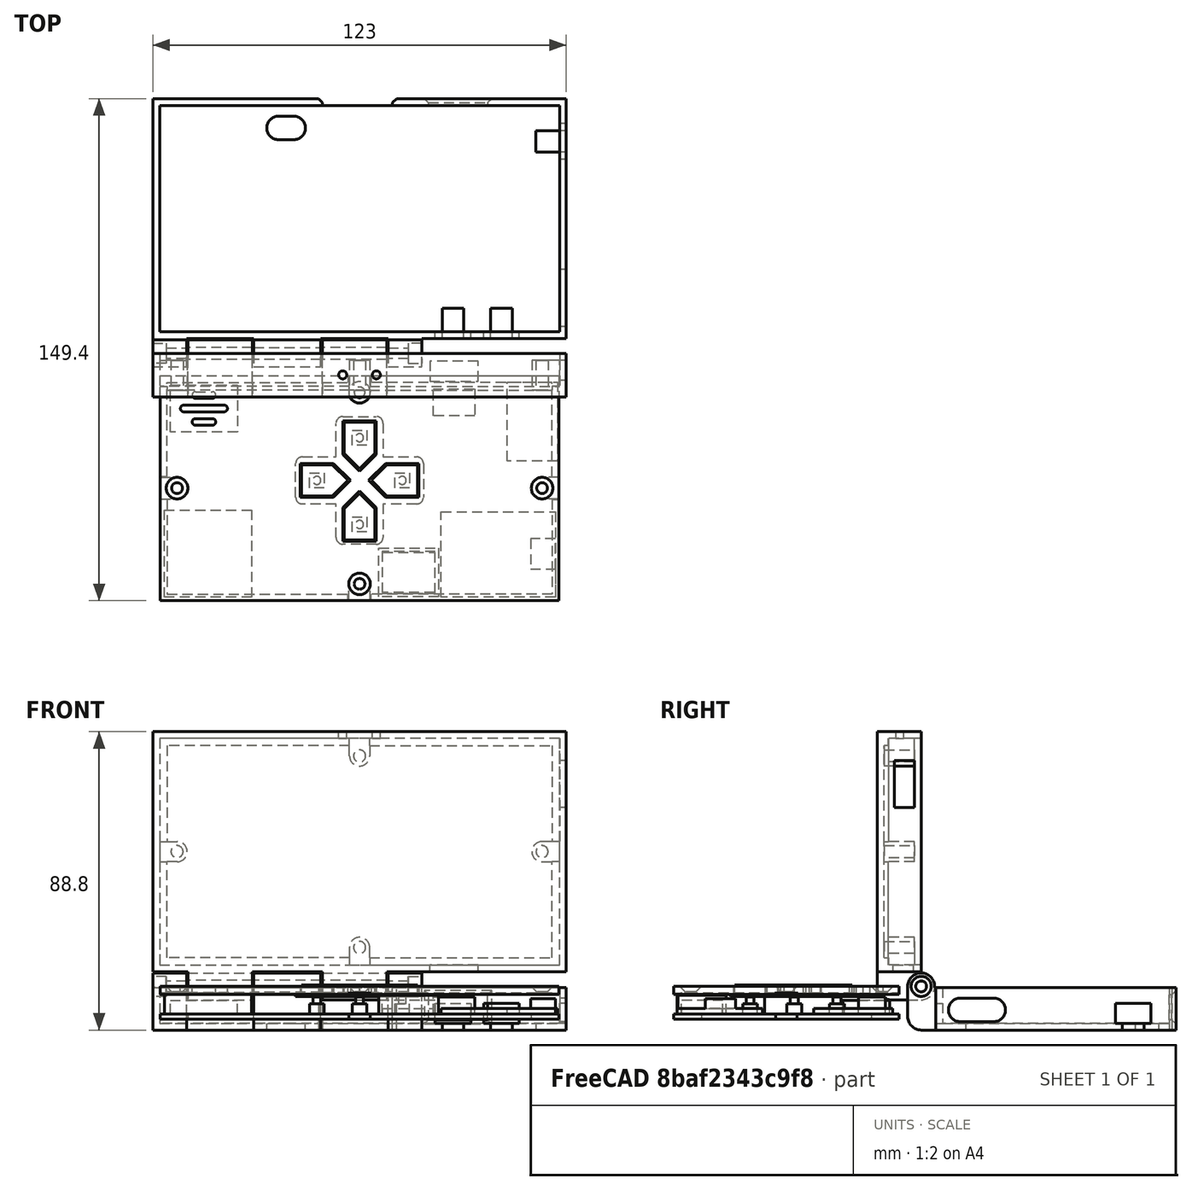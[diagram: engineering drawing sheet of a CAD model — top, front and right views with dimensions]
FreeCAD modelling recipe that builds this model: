
FCSTD DOCUMENT  (FreeCAD 0.19R24276 (Git))
Label: M3
License: All rights reserved
LicenseURL: http://en.wikipedia.org/wiki/All_rights_reserved
objects: Sketcher::SketchObject×45, PartDesign::Pocket×20, PartDesign::ShapeBinder×18, PartDesign::Pad×16, PartDesign::Body×7, TechDraw::DrawViewDimension×6, TechDraw::DrawViewPart×5, Mesh::Feature×5, TechDraw::DrawSVGTemplate×2, PartDesign::Chamfer×2, TechDraw::DrawPage×2
note: 146 computed .brp shape members not serialized (recipe doc carries the construction recipe); baked Part::Feature solids carry a one-line shape summary decoded from their .brp

FEATURE [TechDraw::DrawSVGTemplate] Template
  EditableTexts = Designed_by_Name=Designed by Name; Drawing_number=Drawing number; FC-Date=Date; FC-SC=Scale; FC-SH=Sheet; FC-Title=Title; Subtitle=Subtitle; Weight=Weight
  Height = 210
  Orientation = 1
  Width = 297
FEATURE [Sketcher::SketchObject] Sketch  label="Workspace"
  FullyConstrained = true
  MapMode = 5
  Support = -> [XY_Plane]
  sketch-geometry (8):
    g0: LineSegment StartX=-59.3 StartY=-6.6 StartZ=0 EndX=59.3 EndY=-6.6 EndZ=0
    g1: LineSegment StartX=59.3 StartY=-6.6 StartZ=0 EndX=59.3 EndY=-73.6 EndZ=0
    g2: LineSegment StartX=59.3 StartY=-73.6 StartZ=0 EndX=-59.3 EndY=-73.6 EndZ=0
    g3: LineSegment StartX=-59.3 StartY=-73.6 StartZ=0 EndX=-59.3 EndY=-6.6 EndZ=0
    g4: LineSegment StartX=-59.3 StartY=73.6 StartZ=0 EndX=59.3 EndY=73.6 EndZ=0
    g5: LineSegment StartX=59.3 StartY=73.6 StartZ=0 EndX=59.3 EndY=6.6 EndZ=0
    g6: LineSegment StartX=59.3 StartY=6.6 StartZ=0 EndX=-59.3 EndY=6.6 EndZ=0
    g7: LineSegment StartX=-59.3 StartY=6.6 StartZ=0 EndX=-59.3 EndY=73.6 EndZ=0
  constraints (22):
    c: Coincident(g0,g1)
    c: Coincident(g1,g2)
    c: Coincident(g2,g3)
    c: Coincident(g3,g0)
    c: Horizontal(g2)
    c: Vertical(g1)
    c: Vertical(g3)
    c: Symmetric(g0,g0,g-2)
    c: DistanceY(g1,g1) = 67
    c: DistanceY(g0,g-1) = 6.6
    c: Coincident(g4,g5)
    c: Coincident(g5,g6)
    c: Coincident(g6,g7)
    c: Coincident(g7,g4)
    c: Horizontal(g6)
    c: Vertical(g5)
    c: Vertical(g7)
    c: Equal(g0,g6)
    c: Equal(g1,g5)
    c: DistanceX(g2,g2) = 118.6
    c: DistanceY(g-1,g5) = 6.6
    c: Symmetric(g4,g4,g-2)
FEATURE [Sketcher::SketchObject] Sketch022  label="Key & SD"
  AttachmentOffset = pos=(0,0,-75.2) rot=(0,0,1;0rad)
  FullyConstrained = true
  MapMode = 5
  Placement = pos=(0,75.2,1.67e-14) rot=(1,0,0;1.5708rad)
  Support = -> [XZ_Plane]
  sketch-geometry (8):
    g0: LineSegment StartX=23.5 StartY=-4.5 StartZ=0 EndX=35.1 EndY=-4.5 EndZ=0
    g1: LineSegment StartX=35.1 StartY=-4.5 StartZ=0 EndX=35.1 EndY=-8 EndZ=0
    g2: LineSegment StartX=35.1 StartY=-8 StartZ=0 EndX=23.5 EndY=-8 EndZ=0
    g3: LineSegment StartX=23.5 StartY=-8 StartZ=0 EndX=23.5 EndY=-4.5 EndZ=0
    g4: LineSegment StartX=-8 StartY=-3 StartZ=0 EndX=6.8 EndY=-3 EndZ=0
    g5: LineSegment StartX=6.8 StartY=-3 StartZ=0 EndX=6.8 EndY=-11 EndZ=0
    g6: LineSegment StartX=6.8 StartY=-11 StartZ=0 EndX=-8 EndY=-11 EndZ=0
    g7: LineSegment StartX=-8 StartY=-11 StartZ=0 EndX=-8 EndY=-3 EndZ=0
  constraints (24):
    c: Coincident(g0,g1)
    c: Coincident(g1,g2)
    c: Coincident(g2,g3)
    c: Coincident(g3,g0)
    c: Horizontal(g0)
    c: Horizontal(g2)
    c: Vertical(g1)
    c: Vertical(g3)
    c: Coincident(g4,g5)
    c: Coincident(g5,g6)
    c: Coincident(g6,g7)
    c: Coincident(g7,g4)
    c: Horizontal(g4)
    c: Horizontal(g6)
    c: Vertical(g5)
    c: Vertical(g7)
    c: DistanceX(g0,g0) = 11.6
    c: DistanceX(g4,g4) = 14.8
    c: DistanceY(g7,g7) = 8
    c: DistanceY(g1,g1) = 3.5
    c: DistanceX(g-1,g1) = 35.1
    c: DistanceX(g-1,g5) = 6.8
    c: DistanceY(g1,g-1) = 8
    c: DistanceY(g6,g-1) = 11
FEATURE [Sketcher::SketchObject] Sketch023  label="USB & CONN"
  AttachmentOffset = pos=(0,0,61.5) rot=(0,0,1;0rad)
  ExternalGeometry = -> [Sketch]
  FullyConstrained = true
  MapMode = 5
  Placement = pos=(61.5,-1.37e-14,1.37e-14) rot=(0.57735,0.57735,0.57735;2.0944rad)
  Support = -> [YZ_Plane]
  sketch-geometry (12):
    g0: ArcOfCircle CenterX=11.6 CenterY=-7 CenterZ=0 NormalX=0 NormalY=0 NormalZ=1 AngleXU=0 Radius=3.5 StartAngle=1.5708 EndAngle=4.71239
    g1: ArcOfCircle CenterX=21.6 CenterY=-7 CenterZ=0 NormalX=0 NormalY=0 NormalZ=1 AngleXU=0 Radius=3.5 StartAngle=4.71239 EndAngle=7.85398
    g2: LineSegment StartX=11.6 StartY=-10.5 StartZ=0 EndX=21.6 EndY=-10.5 EndZ=0
    g3: LineSegment StartX=11.6 StartY=-3.5 StartZ=0 EndX=21.6 EndY=-3.5 EndZ=0
    g4: LineSegment StartX=57.8 StartY=-5 StartZ=0 EndX=68.4 EndY=-5 EndZ=0
    g5: LineSegment StartX=68.4 StartY=-5 StartZ=0 EndX=68.4 EndY=-11 EndZ=0
    g6: LineSegment StartX=68.4 StartY=-11 StartZ=0 EndX=66.3 EndY=-11 EndZ=0
    g7: LineSegment StartX=57.8 StartY=-11 StartZ=0 EndX=57.8 EndY=-5 EndZ=0
    g8: LineSegment StartX=66.3 StartY=-11 StartZ=0 EndX=66.3 EndY=-13 EndZ=0
    g9: LineSegment StartX=66.3 StartY=-13 StartZ=0 EndX=59.9 EndY=-13 EndZ=0
    g10: LineSegment StartX=59.9 StartY=-13 StartZ=0 EndX=59.9 EndY=-11 EndZ=0
    g11: LineSegment StartX=59.9 StartY=-11 StartZ=0 EndX=57.8 EndY=-11 EndZ=0
  constraints (33):
    c: Tangent(g0,g3) = 1.5708
    c: Tangent(g0,g2) = -1.5708
    c: Tangent(g2,g1) = -1.5708
    c: Tangent(g3,g1) = 1.5708
    c: Horizontal(g2)
    c: Equal(g0,g1)
    c: Coincident(g4,g5)
    c: Coincident(g5,g6)
    c: Coincident(g11,g7)
    c: Coincident(g7,g4)
    c: Horizontal(g4)
    c: Horizontal(g6)
    c: Vertical(g5)
    c: Vertical(g7)
    c: Coincident(g8,g9)
    c: Coincident(g9,g10)
    c: Horizontal(g9)
    c: Vertical(g8)
    c: Vertical(g10)
    c: Coincident(g6,g8)
    c: Coincident(g11,g10)
    c: Tangent(g6,g11)
    c: Equal(g6,g11)
    c: DistanceX(g9,g9) = 6.4
    c: DistanceX(g4,g4) = 10.6
    c: DistanceY(g5,g5) = 6
    c: DistanceY(g8,g5) = 2
    c: Radius(g1) = 3.5
    c: DistanceX(g0,g1) = 10
    c: DistanceY(g8,g-3) = 13
    c: DistanceX(g4,g-3) = 5.2
    c: DistanceY(g0,g-3) = 7
    c: DistanceX(g-3,g0) = 5
FEATURE [Sketcher::SketchObject] Sketch024  label="CONN 2"
  AttachmentOffset = pos=(0,0,-4.2) rot=(0,0,1;0rad)
  ExternalGeometry = -> [Sketch]
  FullyConstrained = true
  MapMode = 5
  Placement = pos=(0,4.2,9e-16) rot=(1,0,0;1.5708rad)
  Support = -> [XZ_Plane]
  sketch-geometry (16):
    g0: LineSegment StartX=22.5 StartY=-5 StartZ=0 EndX=33.1 EndY=-5 EndZ=0
    g1: LineSegment StartX=33.1 StartY=-5 StartZ=0 EndX=33.1 EndY=-11 EndZ=0
    g2: LineSegment StartX=33.1 StartY=-11 StartZ=0 EndX=31 EndY=-11 EndZ=0
    g3: LineSegment StartX=22.5 StartY=-11 StartZ=0 EndX=22.5 EndY=-5 EndZ=0
    g4: LineSegment StartX=31 StartY=-11 StartZ=0 EndX=31 EndY=-13 EndZ=0
    g5: LineSegment StartX=31 StartY=-13 StartZ=0 EndX=24.6 EndY=-13 EndZ=0
    g6: LineSegment StartX=24.6 StartY=-13 StartZ=0 EndX=24.6 EndY=-11 EndZ=0
    g7: LineSegment StartX=36.9 StartY=-5 StartZ=0 EndX=47.5 EndY=-5 EndZ=0
    g8: LineSegment StartX=47.5 StartY=-5 StartZ=0 EndX=47.5 EndY=-11 EndZ=0
    g9: LineSegment StartX=47.5 StartY=-11 StartZ=0 EndX=45.4 EndY=-11 EndZ=0
    g10: LineSegment StartX=36.9 StartY=-11 StartZ=0 EndX=36.9 EndY=-5 EndZ=0
    g11: LineSegment StartX=45.4 StartY=-11 StartZ=0 EndX=45.4 EndY=-13 EndZ=0
    g12: LineSegment StartX=45.4 StartY=-13 StartZ=0 EndX=39 EndY=-13 EndZ=0
    g13: LineSegment StartX=39 StartY=-13 StartZ=0 EndX=39 EndY=-11 EndZ=0
    g14: LineSegment StartX=24.6 StartY=-11 StartZ=0 EndX=22.5 EndY=-11 EndZ=0
    g15: LineSegment StartX=39 StartY=-11 StartZ=0 EndX=36.9 EndY=-11 EndZ=0
  constraints (46):
    c: Coincident(g0,g1)
    c: Coincident(g1,g2)
    c: Coincident(g14,g3)
    c: Coincident(g3,g0)
    c: Horizontal(g0)
    c: Horizontal(g2)
    c: Vertical(g1)
    c: Vertical(g3)
    c: Coincident(g4,g5)
    c: Coincident(g5,g6)
    c: Horizontal(g5)
    c: Vertical(g4)
    c: Vertical(g6)
    c: Coincident(g7,g8)
    c: Coincident(g8,g9)
    c: Coincident(g15,g10)
    c: Coincident(g10,g7)
    c: Horizontal(g7)
    c: Horizontal(g9)
    c: Vertical(g8)
    c: Vertical(g10)
    c: Coincident(g11,g12)
    c: Coincident(g12,g13)
    c: Horizontal(g12)
    c: Vertical(g11)
    c: Vertical(g13)
    c: Coincident(g2,g4)
    c: Coincident(g14,g6)
    c: Tangent(g2,g14)
    c: Coincident(g9,g11)
    c: Coincident(g15,g13)
    c: Tangent(g9,g15)
    c: Equal(g14,g2)
    c: Equal(g2,g15)
    c: Equal(g15,g9)
    c: Equal(g1,g10)
    c: Equal(g0,g7)
    c: Horizontal(g4,g12)
    c: Horizontal(g1,g10)
    c: DistanceY(g11,g8) = 2
    c: DistanceX(g7,g7) = 10.6
    c: DistanceY(g8,g8) = 6
    c: DistanceX(g12,g12) = 6.4
    c: DistanceY(g11,g-1) = 13
    c: DistanceX(g7,g-3) = 11.8
    c: DistanceX(g0,g-3) = 26.2
FEATURE [Sketcher::SketchObject] Sketch025  label="RESET"
  ExternalGeometry = -> [Sketch]
  FullyConstrained = true
  MapMode = 5
  Support = -> [XY_Plane]
  sketch-geometry (4):
    g0: ArcOfCircle CenterX=-24.1 CenterY=67.1 CenterZ=0 NormalX=0 NormalY=0 NormalZ=1 AngleXU=0 Radius=3.5 StartAngle=1.5708 EndAngle=4.71239
    g1: ArcOfCircle CenterX=-19.6 CenterY=67.1 CenterZ=0 NormalX=0 NormalY=0 NormalZ=1 AngleXU=0 Radius=3.5 StartAngle=4.71239 EndAngle=7.85398
    g2: LineSegment StartX=-24.1 StartY=63.6 StartZ=0 EndX=-19.6 EndY=63.6 EndZ=0
    g3: LineSegment StartX=-24.1 StartY=70.6 StartZ=0 EndX=-19.6 EndY=70.6 EndZ=0
  constraints (10):
    c: Tangent(g0,g3) = 1.5708
    c: Tangent(g0,g2) = -1.5708
    c: Tangent(g2,g1) = -1.5708
    c: Tangent(g3,g1) = 1.5708
    c: Horizontal(g2)
    c: Equal(g0,g1)
    c: Radius(g0) = 3.5
    c: DistanceX(g0,g1) = 4.5
    c: DistanceX(g-3,g0) = 35.2
    c: DistanceY(g0,g-4) = 3
FEATURE [Sketcher::SketchObject] Sketch031  label="FIX HOLE"
  ExternalGeometry = -> [Sketch]
  FullyConstrained = true
  MapMode = 5
  Support = -> [XY_Plane]
  sketch-geometry (32):
    g0: LineSegment StartX=-3 StartY=-8.6 StartZ=0 EndX=3 EndY=-8.6 EndZ=0
    g1: LineSegment StartX=3 StartY=-8.6 StartZ=0 EndX=3 EndY=-11.6 EndZ=0
    g2: LineSegment StartX=2.02025e-10 StartY=-14.6 StartZ=0 EndX=-2.01994e-10 EndY=-14.6 EndZ=0
    g3: LineSegment StartX=-3 StartY=-11.6 StartZ=0 EndX=-3 EndY=-8.6 EndZ=0
    g4: LineSegment StartX=54.3 StartY=-37.1 StartZ=0 EndX=57.3 EndY=-37.1 EndZ=0
    g5: LineSegment StartX=57.3 StartY=-37.1 StartZ=0 EndX=57.3 EndY=-43.1 EndZ=0
    g6: LineSegment StartX=57.3 StartY=-43.1 StartZ=0 EndX=54.3 EndY=-43.1 EndZ=0
    g7: LineSegment StartX=51.3 StartY=-40.1 StartZ=0 EndX=51.3 EndY=-40.1 EndZ=0
    g8: LineSegment StartX=-2.04292e-10 StartY=-65.6 StartZ=0 EndX=2.04323e-10 EndY=-65.6 EndZ=0
    g9: LineSegment StartX=3 StartY=-68.6 StartZ=0 EndX=3 EndY=-71.6 EndZ=0
    g10: LineSegment StartX=3 StartY=-71.6 StartZ=0 EndX=-3 EndY=-71.6 EndZ=0
    g11: LineSegment StartX=-3 StartY=-71.6 StartZ=0 EndX=-3 EndY=-68.6 EndZ=0
    g12: LineSegment StartX=-57.3 StartY=-37.1 StartZ=0 EndX=-54.3 EndY=-37.1 EndZ=0
    g13: LineSegment StartX=-51.3 StartY=-40.1 StartZ=0 EndX=-51.3 EndY=-40.1 EndZ=0
    g14: LineSegment StartX=-54.3 StartY=-43.1 StartZ=0 EndX=-57.3 EndY=-43.1 EndZ=0
    g15: LineSegment StartX=-57.3 StartY=-43.1 StartZ=0 EndX=-57.3 EndY=-37.1 EndZ=0
    g16: ArcOfCircle CenterX=-54.3 CenterY=-40.1 CenterZ=0 NormalX=0 NormalY=0 NormalZ=1 AngleXU=0 Radius=3 StartAngle=5.39571e-11 EndAngle=1.5708
    g17: ArcOfCircle CenterX=-54.3 CenterY=-40.1 CenterZ=0 NormalX=0 NormalY=0 NormalZ=1 AngleXU=0 Radius=3 StartAngle=4.71239 EndAngle=6.28319
    g18: ArcOfCircle CenterX=-4.11221e-11 CenterY=-11.6 CenterZ=0 NormalX=0 NormalY=0 NormalZ=1 AngleXU=0 Radius=3 StartAngle=3.14159 EndAngle=4.71239
    g19: ArcOfCircle CenterX=4.12844e-11 CenterY=-11.6 CenterZ=0 NormalX=0 NormalY=0 NormalZ=1 AngleXU=0 Radius=3 StartAngle=4.71239 EndAngle=6.28319
    g20: ArcOfCircle CenterX=-4.0526e-11 CenterY=-68.6 CenterZ=0 NormalX=0 NormalY=0 NormalZ=1 AngleXU=0 Radius=3 StartAngle=1.5708 EndAngle=3.14159
    g21: ArcOfCircle CenterX=4.0686e-11 CenterY=-68.6 CenterZ=0 NormalX=0 NormalY=0 NormalZ=1 AngleXU=0 Radius=3 StartAngle=5.62494e-11 EndAngle=1.5708
    g22: ArcOfCircle CenterX=54.3 CenterY=-40.1 CenterZ=0 NormalX=0 NormalY=0 NormalZ=1 AngleXU=0 Radius=3 StartAngle=1.5708 EndAngle=3.14159
    g23: ArcOfCircle CenterX=54.3 CenterY=-40.1 CenterZ=0 NormalX=0 NormalY=0 NormalZ=1 AngleXU=0 Radius=3 StartAngle=3.14159 EndAngle=4.71239
    g24: LineSegment StartX=57.3 StartY=-8.6 StartZ=0 EndX=57.3 EndY=-37.1 EndZ=0
    g25: LineSegment StartX=57.3 StartY=-71.6 StartZ=0 EndX=57.3 EndY=-43.1 EndZ=0
    g26: LineSegment StartX=-57.3 StartY=-71.6 StartZ=0 EndX=-3 EndY=-71.6 EndZ=0
    g27: LineSegment StartX=3 StartY=-71.6 StartZ=0 EndX=57.3 EndY=-71.6 EndZ=0
    g28: LineSegment StartX=-57.3 StartY=-71.6 StartZ=0 EndX=-57.3 EndY=-43.1 EndZ=0
    g29: LineSegment StartX=-57.3 StartY=-37.1 StartZ=0 EndX=-57.3 EndY=-8.6 EndZ=0
    g30: LineSegment StartX=-57.3 StartY=-8.6 StartZ=0 EndX=-3 EndY=-8.6 EndZ=0
    g31: LineSegment StartX=3 StartY=-8.6 StartZ=0 EndX=57.3 EndY=-8.6 EndZ=0
  constraints (84):
    c: Coincident(g0,g1)
    c: Coincident(g3,g0)
    c: Horizontal(g0)
    c: Horizontal(g2)
    c: Vertical(g1)
    c: Vertical(g3)
    c: Coincident(g4,g5)
    c: Coincident(g5,g6)
    c: Horizontal(g4)
    c: Horizontal(g6)
    c: Vertical(g5)
    c: Vertical(g7)
    c: Coincident(g9,g10)
    c: Coincident(g10,g11)
    c: Horizontal(g8)
    c: Horizontal(g10)
    c: Vertical(g9)
    c: Vertical(g11)
    c: Coincident(g14,g15)
    c: Coincident(g15,g12)
    c: Horizontal(g12)
    c: Horizontal(g14)
    c: Vertical(g13)
    c: Vertical(g15)
    c: Tangent(g12,g16) = 1.5708
    c: Tangent(g13,g16) = 1.5708
    c: Tangent(g13,g17) = 1.5708
    c: Tangent(g14,g17) = 1.5708
    c: Tangent(g2,g18) = 1.5708
    c: Tangent(g3,g18) = 1.5708
    c: Tangent(g1,g19) = 1.5708
    c: Tangent(g2,g19) = 1.5708
    c: Tangent(g8,g20) = 1.5708
    c: Tangent(g11,g20) = 1.5708
    c: Tangent(g8,g21) = 1.5708
    c: Tangent(g9,g21) = 1.5708
    c: Tangent(g4,g22) = 1.5708
    c: Tangent(g7,g22) = 1.5708
    c: Tangent(g6,g23) = 1.5708
    c: Tangent(g7,g23) = 1.5708
    c: Equal(g16,g17)
    c: Equal(g17,g18)
    c: Equal(g18,g19)
    c: Equal(g19,g20)
    c: Equal(g20,g21)
    c: Equal(g21,g23)
    c: Equal(g23,g22)
    c: Equal(g0,g5)
    c: Equal(g5,g10)
    c: Equal(g10,g15)
    c: Equal(g12,g1)
    c: Equal(g1,g6)
    c: Equal(g6,g11)
    c: DistanceX(g10,g10) = 6
    c: DistanceX(g25,g-5) = 2
    c: DistanceY(g-5,g25) = 2
    c: Coincident(g24,g4)
    c: Vertical(g24)
    c: Coincident(g25,g5)
    c: Vertical(g25)
    c: Equal(g24,g25)
    c: DistanceX(g-3,g29) = 2
    c: DistanceY(g29,g-3) = 2
    c: Coincident(g26,g10)
    c: Horizontal(g26)
    c: Coincident(g27,g9)
    c: Coincident(g27,g25)
    c: Horizontal(g27)
    c: Coincident(g28,g26)
    c: Coincident(g28,g14)
    c: Coincident(g29,g12)
    c: Coincident(g30,g29)
    c: Coincident(g30,g0)
    c: Coincident(g31,g0)
    c: Coincident(g31,g24)
    c: Horizontal(g31)
    c: Horizontal(g30)
    c: Vertical(g29)
    c: Vertical(g28)
    c: Equal(g28,g29)
    c: Equal(g30,g31)
    c: Equal(g26,g27)
    c: Radius(g21) = 3
    c: DistanceY(g9,g9) = 3
FEATURE [Sketcher::SketchObject] Sketch032  label="PARTS"
  ExternalGeometry = -> [Sketch]
  FullyConstrained = true
  MapMode = 5
  Support = -> [XY_Plane]
  sketch-geometry (44):
    g0: LineSegment StartX=6.9 StartY=-59.2 StartZ=0 EndX=22.3 EndY=-59.2 EndZ=0
    g1: LineSegment StartX=22.3 StartY=-59.2 StartZ=0 EndX=22.3 EndY=-71.2 EndZ=0
    g2: LineSegment StartX=22.3 StartY=-71.2 StartZ=0 EndX=6.9 EndY=-71.2 EndZ=0
    g3: LineSegment StartX=6.9 StartY=-71.2 StartZ=0 EndX=6.9 EndY=-59.2 EndZ=0
    g4: LineSegment StartX=-56.3 StartY=-9.4 StartZ=0 EndX=-36.3 EndY=-9.4 EndZ=0
    g5: LineSegment StartX=-36.3 StartY=-9.4 StartZ=0 EndX=-36.3 EndY=-23.4 EndZ=0
    g6: LineSegment StartX=-36.3 StartY=-23.4 StartZ=0 EndX=-56.3 EndY=-23.4 EndZ=0
    g7: LineSegment StartX=-56.3 StartY=-23.4 StartZ=0 EndX=-56.3 EndY=-9.4 EndZ=0
    g8: LineSegment StartX=-58.1 StartY=-46.6 StartZ=0 EndX=-32.1 EndY=-46.6 EndZ=0
    g9: LineSegment StartX=-32.1 StartY=-46.6 StartZ=0 EndX=-32.1 EndY=-72.6 EndZ=0
    g10: LineSegment StartX=-32.1 StartY=-72.6 StartZ=0 EndX=-58.1 EndY=-72.6 EndZ=0
    g11: LineSegment StartX=-58.1 StartY=-72.6 StartZ=0 EndX=-58.1 EndY=-46.6 EndZ=0
    g12: LineSegment StartX=43.9 StartY=-8.5 StartZ=0 EndX=58.9 EndY=-8.5 EndZ=0
    g13: LineSegment StartX=58.9 StartY=-8.5 StartZ=0 EndX=58.9 EndY=-32 EndZ=0
    g14: LineSegment StartX=58.9 StartY=-32 StartZ=0 EndX=43.9 EndY=-32 EndZ=0
    g15: LineSegment StartX=43.9 StartY=-32 StartZ=0 EndX=43.9 EndY=-8.5 EndZ=0
    g16: LineSegment StartX=24.3 StartY=-47.2 StartZ=0 EndX=58.3 EndY=-47.2 EndZ=0
    g17: LineSegment StartX=58.3 StartY=-47.2 StartZ=0 EndX=58.3 EndY=-72.6 EndZ=0
    g18: LineSegment StartX=58.3 StartY=-72.6 StartZ=0 EndX=24.3 EndY=-72.6 EndZ=0
    g19: LineSegment StartX=24.3 StartY=-72.6 StartZ=0 EndX=24.3 EndY=-47.2 EndZ=0
    g20: LineSegment StartX=-59.3 StartY=-6.6 StartZ=0 EndX=59.3 EndY=-6.6 EndZ=0
    g21: LineSegment StartX=59.3 StartY=-6.6 StartZ=0 EndX=59.3 EndY=-73.6 EndZ=0
    g22: LineSegment StartX=59.3 StartY=-73.6 StartZ=0 EndX=-59.3 EndY=-73.6 EndZ=0
    g23: LineSegment StartX=-59.3 StartY=-73.6 StartZ=0 EndX=-59.3 EndY=-6.6 EndZ=0
    g24: LineSegment StartX=21.9 StartY=-10.6 StartZ=0 EndX=34.3 EndY=-10.6 EndZ=0
    g25: LineSegment StartX=34.3 StartY=-10.6 StartZ=0 EndX=34.3 EndY=-18.6 EndZ=0
    g26: LineSegment StartX=34.3 StartY=-18.6 StartZ=0 EndX=21.9 EndY=-18.6 EndZ=0
    g27: LineSegment StartX=21.9 StartY=-18.6 StartZ=0 EndX=21.9 EndY=-10.6 EndZ=0
    g28: LineSegment StartX=2.2 StartY=-22.9 StartZ=0 EndX=-2.2 EndY=-22.9 EndZ=0
    g29: LineSegment StartX=-2.2 StartY=-22.9 StartZ=0 EndX=-2.2 EndY=-27.3 EndZ=0
    g30: LineSegment StartX=-2.2 StartY=-27.3 StartZ=0 EndX=2.2 EndY=-27.3 EndZ=0
    g31: LineSegment StartX=2.2 StartY=-27.3 StartZ=0 EndX=2.2 EndY=-22.9 EndZ=0
    g32: LineSegment StartX=-14.9 StartY=-35.6 StartZ=0 EndX=-10.5 EndY=-35.6 EndZ=0
    g33: LineSegment StartX=-10.5 StartY=-35.6 StartZ=0 EndX=-10.5 EndY=-40 EndZ=0
    g34: LineSegment StartX=-10.5 StartY=-40 StartZ=0 EndX=-14.9 EndY=-40 EndZ=0
    g35: LineSegment StartX=-14.9 StartY=-40 StartZ=0 EndX=-14.9 EndY=-35.6 EndZ=0
    g36: LineSegment StartX=10.5 StartY=-35.6 StartZ=0 EndX=14.9 EndY=-35.6 EndZ=0
    g37: LineSegment StartX=14.9 StartY=-35.6 StartZ=0 EndX=14.9 EndY=-40 EndZ=0
    g38: LineSegment StartX=14.9 StartY=-40 StartZ=0 EndX=10.5 EndY=-40 EndZ=0
    g39: LineSegment StartX=10.5 StartY=-40 StartZ=0 EndX=10.5 EndY=-35.6 EndZ=0
    g40: LineSegment StartX=-2.2 StartY=-48.7 StartZ=0 EndX=2.2 EndY=-48.7 EndZ=0
    g41: LineSegment StartX=2.2 StartY=-48.7 StartZ=0 EndX=2.2 EndY=-53.1 EndZ=0
    g42: LineSegment StartX=2.2 StartY=-53.1 StartZ=0 EndX=-2.2 EndY=-53.1 EndZ=0
    g43: LineSegment StartX=-2.2 StartY=-53.1 StartZ=0 EndX=-2.2 EndY=-48.7 EndZ=0
  constraints (128):
    c: Coincident(g0,g1)
    c: Coincident(g1,g2)
    c: Coincident(g2,g3)
    c: Coincident(g3,g0)
    c: Horizontal(g0)
    c: Horizontal(g2)
    c: Vertical(g1)
    c: Vertical(g3)
    c: Coincident(g4,g5)
    c: Coincident(g5,g6)
    c: Coincident(g6,g7)
    c: Coincident(g7,g4)
    c: Horizontal(g4)
    c: Horizontal(g6)
    c: Vertical(g5)
    c: Vertical(g7)
    c: Coincident(g8,g9)
    c: Coincident(g9,g10)
    c: Coincident(g10,g11)
    c: Coincident(g11,g8)
    c: Horizontal(g8)
    c: Horizontal(g10)
    c: Vertical(g9)
    c: Vertical(g11)
    c: Coincident(g12,g13)
    c: Coincident(g13,g14)
    c: Coincident(g14,g15)
    c: Coincident(g15,g12)
    c: Horizontal(g12)
    c: Horizontal(g14)
    c: Vertical(g13)
    c: Vertical(g15)
    c: Coincident(g16,g17)
    c: Coincident(g18,g19)
    c: Coincident(g19,g16)
    c: Horizontal(g16)
    c: Horizontal(g18)
    c: Vertical(g17)
    c: Vertical(g19)
    c: Coincident(g20,g21)
    c: Coincident(g21,g22)
    c: Coincident(g22,g23)
    c: Coincident(g23,g20)
    c: Horizontal(g20)
    c: Horizontal(g22)
    c: Vertical(g21)
    c: Vertical(g23)
    c: DistanceY(g18,g17) = 25.4
    c: DistanceX(g18,g18) = 34
    c: Equal(g10,g11)
    c: DistanceX(g10,g10) = 26
    c: DistanceY(g13,g13) = 23.5
    c: DistanceX(g12,g12) = 15
    c: DistanceX(g4,g4) = 20
    c: DistanceY(g7,g7) = 14
    c: DistanceY(g3,g3) = 12
    c: Coincident(g20,g-3)
    c: Coincident(g21,g-4)
    c: Coincident(g17,g18)
    c: DistanceX(g2,g2) = 15.4
    c: Coincident(g24,g25)
    c: Coincident(g25,g26)
    c: Coincident(g26,g27)
    c: Coincident(g27,g24)
    c: Horizontal(g24)
    c: Horizontal(g26)
    c: Vertical(g25)
    c: Vertical(g27)
    c: DistanceX(g26,g26) = 12.4
    c: DistanceY(g27,g27) = 8
    c: DistanceY(g4,g20) = 2.8
    c: DistanceX(g20,g4) = 3
    c: DistanceX(g22,g10) = 1.2
    c: DistanceY(g22,g10) = 1
    c: DistanceY(g21,g17) = 1
    c: DistanceX(g17,g21) = 1
    c: DistanceY(g21,g1) = 2.4
    c: DistanceX(g1,g21) = 37
    c: DistanceX(g12,g20) = 0.4
    c: DistanceY(g12,g20) = 1.9
    c: DistanceX(g24,g20) = 25
    c: DistanceY(g24,g20) = 4
    c: Coincident(g28,g29)
    c: Coincident(g29,g30)
    c: Coincident(g30,g31)
    c: Coincident(g31,g28)
    c: Horizontal(g30)
    c: Vertical(g29)
    c: Vertical(g31)
    c: Coincident(g32,g33)
    c: Coincident(g33,g34)
    c: Coincident(g34,g35)
    c: Coincident(g35,g32)
    c: Horizontal(g32)
    c: Horizontal(g34)
    c: Vertical(g33)
    c: Vertical(g35)
    c: Coincident(g36,g37)
    c: Coincident(g37,g38)
    c: Coincident(g38,g39)
    c: Coincident(g39,g36)
    c: Horizontal(g36)
    c: Horizontal(g38)
    c: Vertical(g37)
    c: Vertical(g39)
    c: Coincident(g40,g41)
    c: Coincident(g41,g42)
    c: Coincident(g42,g43)
    c: Coincident(g43,g40)
    c: Horizontal(g40)
    c: Horizontal(g42)
    c: Vertical(g41)
    c: Vertical(g43)
    c: Equal(g35,g32)
    c: Equal(g32,g31)
    c: Equal(g31,g28)
    c: Equal(g28,g39)
    c: Equal(g39,g36)
    c: Equal(g36,g43)
    c: Equal(g43,g40)
    c: DistanceY(g37,g37) = 4.4
    c: Symmetric(g32,g36,g-2)
    c: Vertical(g40,g30)
    c: Symmetric(g28,g28,g-2)
    c: DistanceX(g33,g38) = 21
    c: DistanceY(g40,g29) = 21.4
    c: DistanceY(g32,g20) = 29
    c: DistanceY(g28,g20) = 16.3
FEATURE [Sketcher::SketchObject] Sketch033  label="BODY-DISP"
  FullyConstrained = true
  MapMode = 5
  Placement = pos=(0,0,0) rot=(0.57735,0.57735,0.57735;2.0944rad)
  Support = -> [YZ_Plane]
  sketch-geometry (9):
    g0: Circle CenterX=0 CenterY=1e-15 CenterZ=0 NormalX=0 NormalY=0 NormalZ=1 AngleXU=0 Radius=1.6
    g1: ArcOfCircle CenterX=0 CenterY=1e-15 CenterZ=0 NormalX=0 NormalY=0 NormalZ=1 AngleXU=0 Radius=4 StartAngle=0 EndAngle=3.14159
    g2: LineSegment StartX=4 StartY=1e-15 StartZ=0 EndX=4.4 EndY=0 EndZ=0
    g3: LineSegment StartX=4.4 StartY=0 StartZ=0 EndX=75.8 EndY=0 EndZ=0
    g4: LineSegment StartX=75.8 StartY=0 StartZ=0 EndX=75.8 EndY=-13 EndZ=0
    g5: LineSegment StartX=75.8 StartY=-13 StartZ=0 EndX=4.4 EndY=-13 EndZ=0
    g6: LineSegment StartX=4.4 StartY=-13 StartZ=0 EndX=-2.7e-15 EndY=-13 EndZ=0
    g7: LineSegment StartX=-4 StartY=1e-15 StartZ=0 EndX=-4 EndY=-9 EndZ=0
    g8: ArcOfCircle CenterX=-2.7e-15 CenterY=-9 CenterZ=0 NormalX=0 NormalY=0 NormalZ=1 AngleXU=0 Radius=4 StartAngle=3.14159 EndAngle=4.71239
  constraints (27):
    c: Coincident(g0,g-1)
    c: Coincident(g1,g0)
    c: Horizontal(g1,g0)
    c: Horizontal(g0,g1)
    c: Radius(g0) = 1.6
    c: Radius(g1) = 4
    c: Coincident(g2,g1)
    c: PointOnObject(g2,g-1)
    c: Coincident(g3,g2)
    c: PointOnObject(g3,g-1)
    c: Coincident(g4,g3)
    c: Vertical(g4)
    c: Coincident(g5,g4)
    c: Horizontal(g5)
    c: Coincident(g6,g5)
    c: PointOnObject(g6,g-2)
    c: Horizontal(g6)
    c: Coincident(g7,g1)
    c: Vertical(g7)
    c: Horizontal(g8,g8)
    c: Vertical(g8,g8)
    c: Coincident(g8,g7)
    c: Coincident(g8,g6)
    c: Vertical(g2,g5)
    c: DistanceX(g5,g5) = 71.4
    c: DistanceX(g2,g2) = 0.4
    c: DistanceY(g4,g4) = 13
FEATURE [Sketcher::SketchObject] Sketch034  label="BODY-MAIN"
  FullyConstrained = true
  MapMode = 5
  Placement = pos=(0,0,0) rot=(0.57735,0.57735,0.57735;2.0944rad)
  Support = -> [YZ_Plane]
  sketch-geometry (9):
    g0: Circle CenterX=0 CenterY=0 CenterZ=0 NormalX=0 NormalY=0 NormalZ=1 AngleXU=0 Radius=1.6
    g1: ArcOfCircle CenterX=0 CenterY=0 CenterZ=0 NormalX=0 NormalY=0 NormalZ=1 AngleXU=0 Radius=4 StartAngle=0 EndAngle=3.14159
    g2: LineSegment StartX=-4 StartY=5e-16 StartZ=0 EndX=-4.4 EndY=5e-16 EndZ=0
    g3: LineSegment StartX=-4.4 StartY=5e-16 StartZ=0 EndX=-75.8 EndY=0 EndZ=0
    g4: LineSegment StartX=4 StartY=0 StartZ=0 EndX=4 EndY=-9 EndZ=0
    g5: LineSegment StartX=-75.8 StartY=0 StartZ=0 EndX=-75.8 EndY=-13 EndZ=0
    g6: LineSegment StartX=-75.8 StartY=-13 StartZ=0 EndX=-4.4 EndY=-13 EndZ=0
    g7: LineSegment StartX=-4.4 StartY=-13 StartZ=0 EndX=-9e-16 EndY=-13 EndZ=0
    g8: ArcOfCircle CenterX=0 CenterY=-9 CenterZ=0 NormalX=0 NormalY=0 NormalZ=1 AngleXU=0 Radius=4 StartAngle=4.71239 EndAngle=6.28319
  constraints (27):
    c: Coincident(g0,g-1)
    c: Horizontal(g1,g1)
    c: Coincident(g1,g0)
    c: Coincident(g2,g1)
    c: PointOnObject(g2,g-1)
    c: Horizontal(g2)
    c: Coincident(g3,g2)
    c: PointOnObject(g3,g-1)
    c: Coincident(g4,g1)
    c: Vertical(g4)
    c: Coincident(g5,g3)
    c: Vertical(g5)
    c: Coincident(g6,g5)
    c: Horizontal(g6)
    c: Coincident(g7,g6)
    c: PointOnObject(g7,g-2)
    c: Horizontal(g7)
    c: Radius(g0) = 1.6
    c: Radius(g1) = 4
    c: Vertical(g2,g6)
    c: DistanceX(g6,g6) = 71.4
    c: DistanceX(g2,g1) = 0.4
    c: DistanceY(g5,g5) = 13
    c: Coincident(g4,g8)
    c: Coincident(g8,g7)
    c: PointOnObject(g8,g-2)
    c: Horizontal(g8,g4)
FEATURE [PartDesign::Body] Body
  Group = -> [Sketch033,Sketch034,Sketch,Sketch022,Sketch023,Sketch024,Sketch025,Sketch031,Sketch032]
  Origin = -> Origin
FEATURE [PartDesign::ShapeBinder] ShapeBinder005
  Support = -> [Sketch033]
  TraceSupport = false
FEATURE [Sketcher::SketchObject] Sketch035
  ExternalGeometry = -> [ShapeBinder005]
  FullyConstrained = true
  MapMode = 5
  Placement = pos=(0,0,0) rot=(0.57735,0.57735,0.57735;2.0944rad)
  Support = -> [YZ_Plane005]
  sketch-geometry (8):
    g0: LineSegment StartX=75.8 StartY=2e-16 StartZ=0 EndX=75.8 EndY=-13 EndZ=0
    g1: LineSegment StartX=75.8 StartY=-13 StartZ=0 EndX=0 EndY=-13 EndZ=0
    g2: ArcOfCircle CenterX=0 CenterY=-9 CenterZ=0 NormalX=0 NormalY=0 NormalZ=1 AngleXU=0 Radius=4 StartAngle=3.14159 EndAngle=4.71239
    g3: ArcOfCircle CenterX=0 CenterY=0 CenterZ=0 NormalX=0 NormalY=0 NormalZ=1 AngleXU=0 Radius=4 StartAngle=0 EndAngle=3.14159
    g4: Circle CenterX=0 CenterY=0 CenterZ=0 NormalX=0 NormalY=0 NormalZ=1 AngleXU=0 Radius=1.6
    g5: LineSegment StartX=-4 StartY=5e-16 StartZ=0 EndX=-4 EndY=-9 EndZ=0
    g6: LineSegment StartX=4 StartY=0 StartZ=0 EndX=4.4 EndY=2e-16 EndZ=0
    g7: LineSegment StartX=4.4 StartY=2e-16 StartZ=0 EndX=75.8 EndY=2e-16 EndZ=0
  constraints (19):
    c: Coincident(g0,g-7)
    c: Coincident(g1,g0)
    c: Coincident(g1,g-6)
    c: Coincident(g2,g-6)
    c: Coincident(g2,g1)
    c: Coincident(g2,g-6)
    c: Coincident(g3,g-1)
    c: Coincident(g3,g-4)
    c: Coincident(g4,g3)
    c: Coincident(g5,g3)
    c: Coincident(g5,g2)
    c: Coincident(g6,g3)
    c: Coincident(g6,g-8)
    c: Coincident(g7,g6)
    c: Coincident(g7,g0)
    c: Horizontal(g7)
    c: Horizontal(g3,g3)
    c: Vertical(g0)
    c: Radius(g4) = 1.6
FEATURE [PartDesign::ShapeBinder] ShapeBinder006
  Support = -> [Sketch034]
  TraceSupport = false
FEATURE [Sketcher::SketchObject] Sketch036
  ExternalGeometry = -> [ShapeBinder006]
  FullyConstrained = true
  MapMode = 5
  Placement = pos=(0,0,0) rot=(0.57735,0.57735,0.57735;2.0944rad)
  Support = -> [YZ_Plane006]
  sketch-geometry (9):
    g0: Circle CenterX=-9.43e-14 CenterY=0 CenterZ=0 NormalX=0 NormalY=0 NormalZ=1 AngleXU=0 Radius=9.43e-14
    g1: Circle CenterX=-9.43e-14 CenterY=0 CenterZ=0 NormalX=0 NormalY=0 NormalZ=1 AngleXU=0 Radius=1.8
    g2: ArcOfCircle CenterX=0 CenterY=-9 CenterZ=0 NormalX=0 NormalY=0 NormalZ=1 AngleXU=0 Radius=4 StartAngle=4.71239 EndAngle=6.28319
    g3: LineSegment StartX=4 StartY=0 StartZ=0 EndX=4 EndY=-9 EndZ=0
    g4: LineSegment StartX=-75.8 StartY=-13 StartZ=0 EndX=-75.8 EndY=0 EndZ=0
    g5: LineSegment StartX=-75.8 StartY=-13 StartZ=0 EndX=0 EndY=-13 EndZ=0
    g6: LineSegment StartX=-4.4 StartY=-2e-16 StartZ=0 EndX=-4 EndY=5e-16 EndZ=0
    g7: LineSegment StartX=-4.4 StartY=-2e-16 StartZ=0 EndX=-75.8 EndY=0 EndZ=0
    g8: ArcOfCircle CenterX=-9.43e-14 CenterY=0 CenterZ=0 NormalX=0 NormalY=0 NormalZ=1 AngleXU=0 Radius=4 StartAngle=0 EndAngle=3.14159
  constraints (20):
    c: Coincident(g0,g-1)
    c: Tangent(g0,g-2)
    c: Coincident(g1,g0)
    c: Coincident(g2,g-4)
    c: Coincident(g2,g-4)
    c: Coincident(g3,g2)
    c: Coincident(g4,g-3)
    c: Coincident(g5,g4)
    c: Coincident(g5,g2)
    c: Radius(g1) = 1.8
    c: Vertical(g2,g2)
    c: Coincident(g3,g-5)
    c: Coincident(g6,g-6)
    c: Coincident(g6,g-5)
    c: Coincident(g7,g6)
    c: Coincident(g7,g4)
    c: Coincident(g8,g0)
    c: Coincident(g8,g6)
    c: Coincident(g8,g3)
    c: Coincident(g-6,g4)
FEATURE [PartDesign::Pad] Pad006
  Direction = (1,1,1)
  Length = 61.5
  Length2 = 61.5
  Placement = pos=(0,0,0) rot=(0.57735,0.57735,0.57735;2.0944rad)
  Profile = -> Sketch036
  Type = 4
FEATURE [PartDesign::Pad] Pad
  Direction = (1,1,1)
  Length = 61.5
  Length2 = 61.5
  Placement = pos=(0,0,0) rot=(0.57735,0.57735,0.57735;2.0944rad)
  Profile = -> Sketch035
  Type = 4
FEATURE [Sketcher::SketchObject] Sketch037
  ExternalGeometry = -> [Pad]
  FullyConstrained = true
  MapMode = 5
  Placement = pos=(3.6e-15,-5.7e-15,-13) rot=(0.707107,0.707107,0;3.14159rad)
  Support = -> [Pad]
  sketch-geometry (12):
    g0: LineSegment StartX=-4 StartY=61.5 StartZ=0 EndX=4.4 EndY=61.5 EndZ=0
    g1: LineSegment StartX=4.4 StartY=61.5 StartZ=0 EndX=4.4 EndY=18.5 EndZ=0
    g2: LineSegment StartX=4.4 StartY=18.5 StartZ=0 EndX=-4 EndY=18.5 EndZ=0
    g3: LineSegment StartX=-4 StartY=18.5 StartZ=0 EndX=-4 EndY=61.5 EndZ=0
    g4: LineSegment StartX=-4 StartY=8.5 StartZ=0 EndX=4.4 EndY=8.5 EndZ=0
    g5: LineSegment StartX=4.4 StartY=8.5 StartZ=0 EndX=4.4 EndY=-11.5 EndZ=0
    g6: LineSegment StartX=4.4 StartY=-11.5 StartZ=0 EndX=-4 EndY=-11.5 EndZ=0
    g7: LineSegment StartX=-4 StartY=-11.5 StartZ=0 EndX=-4 EndY=8.5 EndZ=0
    g8: LineSegment StartX=-4 StartY=-31.5 StartZ=0 EndX=4.4 EndY=-31.5 EndZ=0
    g9: LineSegment StartX=4.4 StartY=-31.5 StartZ=0 EndX=4.4 EndY=-51.5 EndZ=0
    g10: LineSegment StartX=4.4 StartY=-51.5 StartZ=0 EndX=-4 EndY=-51.5 EndZ=0
    g11: LineSegment StartX=-4 StartY=-51.5 StartZ=0 EndX=-4 EndY=-31.5 EndZ=0
  constraints (35):
    c: Coincident(g0,g1)
    c: Coincident(g1,g2)
    c: Coincident(g2,g3)
    c: Coincident(g3,g0)
    c: Horizontal(g0)
    c: Horizontal(g2)
    c: Vertical(g1)
    c: Vertical(g3)
    c: Coincident(g0,g-3)
    c: PointOnObject(g1,g-4)
    c: Coincident(g4,g5)
    c: Coincident(g5,g6)
    c: Coincident(g6,g7)
    c: Coincident(g7,g4)
    c: Horizontal(g4)
    c: Horizontal(g6)
    c: Vertical(g5)
    c: Vertical(g7)
    c: PointOnObject(g4,g-3)
    c: PointOnObject(g5,g-4)
    c: Coincident(g8,g9)
    c: Coincident(g9,g10)
    c: Coincident(g10,g11)
    c: Coincident(g11,g8)
    c: Horizontal(g8)
    c: Horizontal(g10)
    c: Vertical(g9)
    c: Vertical(g11)
    c: PointOnObject(g8,g-3)
    c: PointOnObject(g9,g-4)
    c: DistanceY(g-3,g10) = 10
    c: DistanceY(g-3,g8) = 30
    c: DistanceY(g-3,g6) = 50
    c: DistanceY(g-3,g4) = 70
    c: DistanceY(g-3,g2) = 80
FEATURE [PartDesign::Pocket] Pocket007
  BaseFeature = -> Pad
  Length = 5
  Length2 = 100
  Placement = pos=(0,0,0) rot=(0.57735,0.57735,0.57735;2.0944rad)
  Profile = -> Sketch037
  Type = 1
FEATURE [Sketcher::SketchObject] Sketch038
  ExternalGeometry = -> [Pocket007]
  FullyConstrained = true
  MapMode = 5
  Placement = pos=(18.5,-4.1e-15,1.13e-14) rot=(0.57735,0.57735,0.57735;2.0944rad)
  Support = -> [Pocket007]
  sketch-geometry (1):
    g0: Circle CenterX=0 CenterY=0 CenterZ=0 NormalX=0 NormalY=0 NormalZ=1 AngleXU=0 Radius=3
  constraints (2):
    c: Coincident(g0,g-1)
    c: Radius(g0) = 3
FEATURE [PartDesign::Pocket] Pocket008
  BaseFeature = -> Pocket007
  Length = 4
  Length2 = 100
  Placement = pos=(0,0,0) rot=(0.57735,0.57735,0.57735;2.0944rad)
  Profile = -> Sketch038
  Type = 0
FEATURE [Sketcher::SketchObject] Sketch039
  ExternalGeometry = -> [Pocket008]
  FullyConstrained = true
  MapMode = 5
  Placement = pos=(-61.5,1.35e-14,-1.35e-14) rot=(0.57735,0.57735,-0.57735;4.18879rad)
  Support = -> [Pocket008]
  sketch-geometry (1):
    g0: Circle CenterX=0 CenterY=0 CenterZ=0 NormalX=0 NormalY=0 NormalZ=1 AngleXU=0 Radius=3
  constraints (2):
    c: Coincident(g0,g-1)
    c: Radius(g0) = 3
FEATURE [PartDesign::Pocket] Pocket009
  BaseFeature = -> Pocket008
  Length = 4
  Length2 = 100
  Placement = pos=(0,0,0) rot=(0.57735,0.57735,0.57735;2.0944rad)
  Profile = -> Sketch039
  Type = 0
FEATURE [Sketcher::SketchObject] Sketch040
  ExternalGeometry = -> [Pad006]
  FullyConstrained = true
  MapMode = 5
  Placement = pos=(3.6e-15,-4.8e-15,-13) rot=(0.707107,0.707107,0;3.14159rad)
  Support = -> [Pad006]
  sketch-geometry (12):
    g0: LineSegment StartX=-4.4 StartY=61.5 StartZ=0 EndX=4 EndY=61.5 EndZ=0
    g1: LineSegment StartX=4 StartY=61.5 StartZ=0 EndX=4 EndY=8.1 EndZ=0
    g2: LineSegment StartX=4 StartY=8.1 StartZ=0 EndX=-4.4 EndY=8.1 EndZ=0
    g3: LineSegment StartX=-4.4 StartY=8.1 StartZ=0 EndX=-4.4 EndY=61.5 EndZ=0
    g4: LineSegment StartX=-4.4 StartY=-61.5 StartZ=0 EndX=4 EndY=-61.5 EndZ=0
    g5: LineSegment StartX=4 StartY=-61.5 StartZ=0 EndX=4 EndY=-51.1 EndZ=0
    g6: LineSegment StartX=4 StartY=-51.1 StartZ=0 EndX=-4.4 EndY=-51.1 EndZ=0
    g7: LineSegment StartX=-4.4 StartY=-51.1 StartZ=0 EndX=-4.4 EndY=-61.5 EndZ=0
    g8: LineSegment StartX=-4.4 StartY=-31.9 StartZ=0 EndX=4 EndY=-31.9 EndZ=0
    g9: LineSegment StartX=4 StartY=-31.9 StartZ=0 EndX=4 EndY=-11.1 EndZ=0
    g10: LineSegment StartX=4 StartY=-11.1 StartZ=0 EndX=-4.4 EndY=-11.1 EndZ=0
    g11: LineSegment StartX=-4.4 StartY=-11.1 StartZ=0 EndX=-4.4 EndY=-31.9 EndZ=0
  constraints (34):
    c: Coincident(g0,g1)
    c: Coincident(g1,g2)
    c: Coincident(g2,g3)
    c: Coincident(g3,g0)
    c: Horizontal(g0)
    c: Horizontal(g2)
    c: Vertical(g1)
    c: Vertical(g3)
    c: Coincident(g0,g-3)
    c: PointOnObject(g1,g-4)
    c: Coincident(g4,g5)
    c: Coincident(g5,g6)
    c: Coincident(g6,g7)
    c: Coincident(g7,g4)
    c: Horizontal(g4)
    c: Horizontal(g6)
    c: Vertical(g5)
    c: Vertical(g7)
    c: Coincident(g4,g-3)
    c: PointOnObject(g5,g-4)
    c: Coincident(g8,g9)
    c: Coincident(g9,g10)
    c: Coincident(g10,g11)
    c: Coincident(g11,g8)
    c: Horizontal(g8)
    c: Horizontal(g10)
    c: Vertical(g9)
    c: Vertical(g11)
    c: PointOnObject(g8,g-3)
    c: PointOnObject(g9,g-4)
    c: DistanceY(g4,g5) = 10.4
    c: DistanceY(g4,g8) = 29.6
    c: DistanceY(g4,g9) = 50.4
    c: DistanceY(g4,g1) = 69.6
FEATURE [PartDesign::Pocket] Pocket010
  BaseFeature = -> Pad006
  Length = 5
  Length2 = 100
  Placement = pos=(0,0,0) rot=(0.57735,0.57735,0.57735;2.0944rad)
  Profile = -> Sketch040
  Type = 1
FEATURE [PartDesign::ShapeBinder] ShapeBinder007
  Support = -> [Sketch]
  TraceSupport = false
FEATURE [PartDesign::ShapeBinder] ShapeBinder008
  Support = -> [Sketch025]
  TraceSupport = false
FEATURE [PartDesign::ShapeBinder] ShapeBinder009
  Support = -> [Sketch022]
  TraceSupport = false
FEATURE [PartDesign::ShapeBinder] ShapeBinder010
  Support = -> [Sketch023]
  TraceSupport = false
FEATURE [PartDesign::ShapeBinder] ShapeBinder011
  Support = -> [Sketch024]
  TraceSupport = false
FEATURE [Sketcher::SketchObject] Sketch041
  ExternalGeometry = -> [ShapeBinder007]
  FullyConstrained = true
  MapMode = 5
  Placement = pos=(0,0,3e-16) rot=(0,0,-1;1.5708rad)
  Support = -> [Pocket009]
  sketch-geometry (4):
    g0: LineSegment StartX=-73.8 StartY=59.5 StartZ=0 EndX=-6.4 EndY=59.5 EndZ=0
    g1: LineSegment StartX=-6.4 StartY=59.5 StartZ=0 EndX=-6.4 EndY=-59.5 EndZ=0
    g2: LineSegment StartX=-6.4 StartY=-59.5 StartZ=0 EndX=-73.8 EndY=-59.5 EndZ=0
    g3: LineSegment StartX=-73.8 StartY=-59.5 StartZ=0 EndX=-73.8 EndY=59.5 EndZ=0
  constraints (12):
    c: Coincident(g0,g1)
    c: Coincident(g1,g2)
    c: Coincident(g2,g3)
    c: Coincident(g3,g0)
    c: Horizontal(g0)
    c: Horizontal(g2)
    c: Vertical(g1)
    c: Vertical(g3)
    c: DistanceX(g-4,g1) = 0.2
    c: DistanceY(g1,g-4) = 0.2
    c: DistanceY(g-3,g0) = 0.2
    c: DistanceX(g0,g-3) = 0.2
FEATURE [PartDesign::Pocket] Pocket011
  BaseFeature = -> Pocket009
  Length = 11
  Length2 = 100
  Placement = pos=(0,0,0) rot=(0.57735,0.57735,0.57735;2.0944rad)
  Profile = -> Sketch041
  Type = 0
FEATURE [Sketcher::SketchObject] Sketch042
  ExternalGeometry = -> [ShapeBinder008]
  FullyConstrained = true
  MapMode = 5
  Placement = pos=(1.53e-14,-9.8e-15,-11) rot=(0,0,-1;1.5708rad)
  Support = -> [Pocket011]
  sketch-geometry (4):
    g0: ArcOfCircle CenterX=-67.1 CenterY=-19.6 CenterZ=0 NormalX=0 NormalY=0 NormalZ=1 AngleXU=0 Radius=3.5 StartAngle=1.42e-14 EndAngle=3.14159
    g1: ArcOfCircle CenterX=-67.1 CenterY=-24.1 CenterZ=0 NormalX=0 NormalY=0 NormalZ=1 AngleXU=0 Radius=3.5 StartAngle=3.14159 EndAngle=6.28319
    g2: LineSegment StartX=-70.6 StartY=-19.6 StartZ=0 EndX=-70.6 EndY=-24.1 EndZ=0
    g3: LineSegment StartX=-63.6 StartY=-19.6 StartZ=0 EndX=-63.6 EndY=-24.1 EndZ=0
  constraints (8):
    c: Tangent(g0,g3) = 1.5708
    c: Tangent(g0,g2) = -1.5708
    c: Tangent(g2,g1) = -1.5708
    c: Tangent(g3,g1) = 1.5708
    c: Vertical(g2)
    c: Equal(g0,g1)
    c: Coincident(g0,g-3)
    c: Coincident(g-4,g1)
FEATURE [PartDesign::Pocket] Pocket012
  BaseFeature = -> Pocket011
  Length = 2
  Length2 = 100
  Placement = pos=(0,0,0) rot=(0.57735,0.57735,0.57735;2.0944rad)
  Profile = -> Sketch042
  Type = 0
FEATURE [Sketcher::SketchObject] Sketch043
  ExternalGeometry = -> [ShapeBinder009]
  FullyConstrained = true
  MapMode = 5
  Placement = pos=(3.34e-14,75.8,-1.67e-14) rot=(0.57735,0.57735,0.57735;4.18879rad)
  Support = -> [Pocket012]
  sketch-geometry (8):
    g0: LineSegment StartX=-10 StartY=38.1 StartZ=0 EndX=-2.5 EndY=38.1 EndZ=0
    g1: LineSegment StartX=-2.5 StartY=38.1 StartZ=0 EndX=-2.5 EndY=20.5 EndZ=0
    g2: LineSegment StartX=-2.5 StartY=20.5 StartZ=0 EndX=-10 EndY=20.5 EndZ=0
    g3: LineSegment StartX=-10 StartY=20.5 StartZ=0 EndX=-10 EndY=38.1 EndZ=0
    g4: LineSegment StartX=-13 StartY=9.8 StartZ=0 EndX=2 EndY=9.8 EndZ=0
    g5: LineSegment StartX=2 StartY=9.8 StartZ=0 EndX=2 EndY=-11 EndZ=0
    g6: LineSegment StartX=2 StartY=-11 StartZ=0 EndX=-13 EndY=-11 EndZ=0
    g7: LineSegment StartX=-13 StartY=-11 StartZ=0 EndX=-13 EndY=9.8 EndZ=0
  constraints (24):
    c: Coincident(g0,g1)
    c: Coincident(g1,g2)
    c: Coincident(g2,g3)
    c: Coincident(g3,g0)
    c: Horizontal(g0)
    c: Horizontal(g2)
    c: Vertical(g1)
    c: Vertical(g3)
    c: Coincident(g4,g5)
    c: Coincident(g5,g6)
    c: Coincident(g6,g7)
    c: Coincident(g7,g4)
    c: Horizontal(g4)
    c: Horizontal(g6)
    c: Vertical(g5)
    c: Vertical(g7)
    c: DistanceY(g-3,g0) = 3
    c: DistanceX(g0,g-3) = 2
    c: DistanceX(g-4,g1) = 2
    c: DistanceY(g1,g-4) = 3
    c: DistanceX(g4,g-5) = 2
    c: DistanceY(g-5,g4) = 3
    c: DistanceY(g5,g-6) = 3
    c: DistanceX(g-6,g5) = 5
FEATURE [PartDesign::Pocket] Pocket013
  BaseFeature = -> Pocket012
  Length = 2
  Length2 = 100
  Placement = pos=(0,0,0) rot=(0.57735,0.57735,0.57735;2.0944rad)
  Profile = -> Sketch043
  Type = 0
FEATURE [Sketcher::SketchObject] Sketch044
  ExternalGeometry = -> [ShapeBinder010]
  FullyConstrained = true
  MapMode = 5
  Placement = pos=(61.5,-1.35e-14,1.35e-14) rot=(0.57735,0.57735,0.57735;2.0944rad)
  Support = -> [Pocket013]
  sketch-geometry (12):
    g0: ArcOfCircle CenterX=11.6 CenterY=-7 CenterZ=0 NormalX=0 NormalY=0 NormalZ=1 AngleXU=0 Radius=3.5 StartAngle=1.5708 EndAngle=4.71239
    g1: ArcOfCircle CenterX=21.6 CenterY=-7 CenterZ=0 NormalX=0 NormalY=0 NormalZ=1 AngleXU=0 Radius=3.5 StartAngle=4.71239 EndAngle=7.85398
    g2: LineSegment StartX=11.6 StartY=-10.5 StartZ=0 EndX=21.6 EndY=-10.5 EndZ=0
    g3: LineSegment StartX=11.6 StartY=-3.5 StartZ=0 EndX=21.6 EndY=-3.5 EndZ=0
    g4: LineSegment StartX=57.8 StartY=-5 StartZ=0 EndX=68.4 EndY=-5 EndZ=0
    g5: LineSegment StartX=68.4 StartY=-5 StartZ=0 EndX=68.4 EndY=-11 EndZ=0
    g6: LineSegment StartX=68.4 StartY=-11 StartZ=0 EndX=66.3 EndY=-11 EndZ=0
    g7: LineSegment StartX=66.3 StartY=-11 StartZ=0 EndX=66.3 EndY=-13 EndZ=0
    g8: LineSegment StartX=66.3 StartY=-13 StartZ=0 EndX=59.9 EndY=-13 EndZ=0
    g9: LineSegment StartX=59.9 StartY=-13 StartZ=0 EndX=59.9 EndY=-11 EndZ=0
    g10: LineSegment StartX=59.9 StartY=-11 StartZ=0 EndX=57.8 EndY=-11 EndZ=0
    g11: LineSegment StartX=57.8 StartY=-11 StartZ=0 EndX=57.8 EndY=-5 EndZ=0
  constraints (24):
    c: Tangent(g0,g3) = 1.5708
    c: Tangent(g0,g2) = -1.5708
    c: Tangent(g2,g1) = -1.5708
    c: Tangent(g3,g1) = 1.5708
    c: Horizontal(g2)
    c: Equal(g0,g1)
    c: Coincident(g0,g-3)
    c: Coincident(g1,g-4)
    c: Coincident(g4,g-5)
    c: Coincident(g4,g-6)
    c: Coincident(g5,g4)
    c: Coincident(g5,g-6)
    c: Coincident(g6,g5)
    c: Coincident(g6,g-7)
    c: Coincident(g7,g6)
    c: Coincident(g7,g-7)
    c: Coincident(g8,g7)
    c: Coincident(g8,g-8)
    c: Coincident(g9,g8)
    c: Coincident(g9,g-8)
    c: Coincident(g10,g9)
    c: Coincident(g10,g-5)
    c: Coincident(g11,g10)
    c: Coincident(g11,g4)
FEATURE [PartDesign::Pocket] Pocket014
  BaseFeature = -> Pocket013
  Length = 9
  Length2 = 100
  Placement = pos=(0,0,0) rot=(0.57735,0.57735,0.57735;2.0944rad)
  Profile = -> Sketch044
  Type = 0
FEATURE [Sketcher::SketchObject] Sketch045
  ExternalGeometry = -> [ShapeBinder011]
  FullyConstrained = true
  MapMode = 5
  Placement = pos=(1.9e-15,4.4,-2.5e-15) rot=(0.57735,0.57735,-0.57735;2.0944rad)
  Support = -> [Pocket014]
  sketch-geometry (16):
    g0: LineSegment StartX=5 StartY=33.1 StartZ=0 EndX=5 EndY=22.5 EndZ=0
    g1: LineSegment StartX=5 StartY=22.5 StartZ=0 EndX=11 EndY=22.5 EndZ=0
    g2: LineSegment StartX=11 StartY=22.5 StartZ=0 EndX=11 EndY=24.6 EndZ=0
    g3: LineSegment StartX=11 StartY=24.6 StartZ=0 EndX=13 EndY=24.6 EndZ=0
    g4: LineSegment StartX=13 StartY=24.6 StartZ=0 EndX=13 EndY=31 EndZ=0
    g5: LineSegment StartX=13 StartY=31 StartZ=0 EndX=11 EndY=31 EndZ=0
    g6: LineSegment StartX=11 StartY=31 StartZ=0 EndX=11 EndY=33.1 EndZ=0
    g7: LineSegment StartX=11 StartY=33.1 StartZ=0 EndX=5 EndY=33.1 EndZ=0
    g8: LineSegment StartX=5 StartY=36.9 StartZ=0 EndX=11 EndY=36.9 EndZ=0
    g9: LineSegment StartX=11 StartY=36.9 StartZ=0 EndX=11 EndY=39 EndZ=0
    g10: LineSegment StartX=11 StartY=39 StartZ=0 EndX=13 EndY=39 EndZ=0
    g11: LineSegment StartX=13 StartY=39 StartZ=0 EndX=13 EndY=45.4 EndZ=0
    g12: LineSegment StartX=13 StartY=45.4 StartZ=0 EndX=11 EndY=45.4 EndZ=0
    g13: LineSegment StartX=11 StartY=45.4 StartZ=0 EndX=11 EndY=47.5 EndZ=0
    g14: LineSegment StartX=11 StartY=47.5 StartZ=0 EndX=5 EndY=47.5 EndZ=0
    g15: LineSegment StartX=5 StartY=47.5 StartZ=0 EndX=5 EndY=36.9 EndZ=0
  constraints (32):
    c: Coincident(g0,g-7)
    c: Coincident(g0,g-10)
    c: Coincident(g1,g0)
    c: Coincident(g1,g-10)
    c: Coincident(g2,g1)
    c: Coincident(g2,g-9)
    c: Coincident(g3,g2)
    c: Coincident(g3,g-9)
    c: Coincident(g4,g3)
    c: Coincident(g4,g-8)
    c: Coincident(g5,g4)
    c: Coincident(g5,g-8)
    c: Coincident(g6,g5)
    c: Coincident(g6,g-7)
    c: Coincident(g7,g6)
    c: Coincident(g7,g0)
    c: Coincident(g8,g-6)
    c: Coincident(g8,g-6)
    c: Coincident(g9,g8)
    c: Coincident(g9,g-5)
    c: Coincident(g10,g9)
    c: Coincident(g10,g-5)
    c: Coincident(g11,g10)
    c: Coincident(g11,g-4)
    c: Coincident(g12,g11)
    c: Coincident(g12,g-4)
    c: Coincident(g13,g12)
    c: Coincident(g13,g-3)
    c: Coincident(g14,g13)
    c: Coincident(g14,g-3)
    c: Coincident(g15,g14)
    c: Coincident(g15,g8)
FEATURE [PartDesign::Pocket] Pocket015
  BaseFeature = -> Pocket014
  Length = 9
  Length2 = 100
  Placement = pos=(0,0,0) rot=(0.57735,0.57735,0.57735;2.0944rad)
  Profile = -> Sketch045
  Type = 0
FEATURE [PartDesign::Chamfer] Chamfer
  Angle = 45
  Base = -> Pocket015 [Edge102,Edge36,Edge108,Edge107,Edge106,Edge105]
  BaseFeature = -> Pocket015
  ChamferType = 0
  FlipDirection = false
  Placement = pos=(0,0,0) rot=(0.57735,0.57735,0.57735;2.0944rad)
  Size = 1.2
  Size2 = 1
  SupportTransform = false
FEATURE [PartDesign::ShapeBinder] ShapeBinder
  Support = -> [Sketch]
  TraceSupport = false
FEATURE [PartDesign::ShapeBinder] ShapeBinder012
  Support = -> [Sketch031]
  TraceSupport = false
FEATURE [Sketcher::SketchObject] Sketch046
  ExternalGeometry = -> [ShapeBinder]
  FullyConstrained = true
  MapMode = 5
  Placement = pos=(0,0,-1e-16) rot=(0,0,-1;1.5708rad)
  Support = -> [Pocket010]
  sketch-geometry (4):
    g0: LineSegment StartX=6.4 StartY=59.5 StartZ=0 EndX=73.8 EndY=59.5 EndZ=0
    g1: LineSegment StartX=73.8 StartY=59.5 StartZ=0 EndX=73.8 EndY=-59.5 EndZ=0
    g2: LineSegment StartX=73.8 StartY=-59.5 StartZ=0 EndX=6.4 EndY=-59.5 EndZ=0
    g3: LineSegment StartX=6.4 StartY=-59.5 StartZ=0 EndX=6.4 EndY=59.5 EndZ=0
  constraints (12):
    c: Coincident(g0,g1)
    c: Coincident(g1,g2)
    c: Coincident(g2,g3)
    c: Coincident(g3,g0)
    c: Horizontal(g0)
    c: Horizontal(g2)
    c: Vertical(g1)
    c: Vertical(g3)
    c: DistanceY(g1,g-4) = 0.2
    c: DistanceX(g-4,g1) = 0.2
    c: DistanceX(g0,g-3) = 0.2
    c: DistanceY(g-3,g0) = 0.2
FEATURE [PartDesign::Pocket] Pocket
  BaseFeature = -> Pocket010
  Length = 2
  Length2 = 100
  Placement = pos=(0,0,0) rot=(0.57735,0.57735,0.57735;2.0944rad)
  Profile = -> Sketch046
  Type = 0
FEATURE [Sketcher::SketchObject] Sketch047
  ExternalGeometry = -> [ShapeBinder]
  FullyConstrained = true
  MapMode = 5
  Placement = pos=(1.4e-15,-1.3e-15,-2) rot=(0,0,-1;1.5708rad)
  Support = -> [Pocket]
  sketch-geometry (4):
    g0: LineSegment StartX=8.6 StartY=57.3 StartZ=0 EndX=71.6 EndY=57.3 EndZ=0
    g1: LineSegment StartX=71.6 StartY=57.3 StartZ=0 EndX=71.6 EndY=-57.3 EndZ=0
    g2: LineSegment StartX=71.6 StartY=-57.3 StartZ=0 EndX=8.6 EndY=-57.3 EndZ=0
    g3: LineSegment StartX=8.6 StartY=-57.3 StartZ=0 EndX=8.6 EndY=57.3 EndZ=0
  constraints (12):
    c: Coincident(g0,g1)
    c: Coincident(g1,g2)
    c: Coincident(g2,g3)
    c: Coincident(g3,g0)
    c: Horizontal(g0)
    c: Horizontal(g2)
    c: Vertical(g1)
    c: Vertical(g3)
    c: DistanceX(g-3,g0) = 2
    c: DistanceY(g0,g-3) = 2
    c: DistanceY(g-4,g1) = 2
    c: DistanceX(g1,g-4) = 2
FEATURE [PartDesign::Pocket] Pocket016
  BaseFeature = -> Pocket
  Length = 9
  Length2 = 100
  Placement = pos=(0,0,0) rot=(0.57735,0.57735,0.57735;2.0944rad)
  Profile = -> Sketch047
  Type = 0
FEATURE [Sketcher::SketchObject] Sketch048
  ExternalGeometry = -> [ShapeBinder012]
  FullyConstrained = true
  MapMode = 5
  Placement = pos=(1.15e-14,-8.6e-15,-11) rot=(0,0,-1;1.5708rad)
  Support = -> [Pocket016]
  sketch-geometry (20):
    g0: Circle CenterX=11.6 CenterY=-4.11195e-11 CenterZ=0 NormalX=0 NormalY=0 NormalZ=1 AngleXU=0 Radius=1.8
    g1: Circle CenterX=68.6 CenterY=-4.05108e-11 CenterZ=0 NormalX=0 NormalY=0 NormalZ=1 AngleXU=0 Radius=1.8
    g2: Circle CenterX=40.1 CenterY=54.3 CenterZ=0 NormalX=0 NormalY=0 NormalZ=1 AngleXU=0 Radius=1.8
    g3: Circle CenterX=40.1 CenterY=-54.3 CenterZ=0 NormalX=0 NormalY=0 NormalZ=1 AngleXU=0 Radius=1.8
    g4: ArcOfCircle CenterX=40.1 CenterY=-54.3 CenterZ=0 NormalX=0 NormalY=0 NormalZ=1 AngleXU=0 Radius=3 StartAngle=4.83868e-11 EndAngle=3.14159
    g5: ArcOfCircle CenterX=11.6 CenterY=-4.11195e-11 CenterZ=0 NormalX=0 NormalY=0 NormalZ=1 AngleXU=0 Radius=3 StartAngle=4.71239 EndAngle=7.85398
    g6: ArcOfCircle CenterX=68.6 CenterY=-4.05108e-11 CenterZ=0 NormalX=0 NormalY=0 NormalZ=1 AngleXU=0 Radius=3 StartAngle=1.5708 EndAngle=4.71239
    g7: ArcOfCircle CenterX=40.1 CenterY=54.3 CenterZ=0 NormalX=0 NormalY=0 NormalZ=1 AngleXU=0 Radius=3 StartAngle=3.14159 EndAngle=6.28319
    g8: LineSegment StartX=37.1 StartY=-54.3 StartZ=0 EndX=37.1 EndY=-57.3 EndZ=0
    g9: LineSegment StartX=37.1 StartY=-57.3 StartZ=0 EndX=43.1 EndY=-57.3 EndZ=0
    g10: LineSegment StartX=43.1 StartY=-57.3 StartZ=0 EndX=43.1 EndY=-54.3 EndZ=0
    g11: LineSegment StartX=68.6 StartY=-3 StartZ=0 EndX=71.6 EndY=-3 EndZ=0
    g12: LineSegment StartX=71.6 StartY=-3 StartZ=0 EndX=71.6 EndY=3 EndZ=0
    g13: LineSegment StartX=71.6 StartY=3 StartZ=0 EndX=68.6 EndY=3 EndZ=0
    g14: LineSegment StartX=11.6 StartY=-3 StartZ=0 EndX=8.6 EndY=-3 EndZ=0
    g15: LineSegment StartX=8.6 StartY=-3 StartZ=0 EndX=8.6 EndY=3 EndZ=0
    g16: LineSegment StartX=8.6 StartY=3 StartZ=0 EndX=11.6 EndY=3 EndZ=0
    g17: LineSegment StartX=37.1 StartY=54.3 StartZ=0 EndX=37.1 EndY=57.3 EndZ=0
    g18: LineSegment StartX=37.1 StartY=57.3 StartZ=0 EndX=43.1 EndY=57.3 EndZ=0
    g19: LineSegment StartX=43.1 StartY=57.3 StartZ=0 EndX=43.1 EndY=54.3 EndZ=0
  constraints (44):
    c: Coincident(g0,g-5)
    c: Coincident(g1,g-10)
    c: Coincident(g2,g-7)
    c: Coincident(g3,g-14)
    c: Coincident(g4,g3)
    c: Coincident(g4,g-15)
    c: Coincident(g4,g-13)
    c: Coincident(g5,g0)
    c: Coincident(g5,g-4)
    c: Coincident(g5,g-5)
    c: Coincident(g6,g1)
    c: Coincident(g6,g-9)
    c: Coincident(g6,g-10)
    c: Coincident(g7,g2)
    c: Coincident(g7,g-7)
    c: Coincident(g7,g-6)
    c: Equal(g2,g1)
    c: Equal(g1,g0)
    c: Equal(g0,g3)
    c: Radius(g3) = 1.8
    c: Coincident(g8,g4)
    c: Coincident(g8,g-12)
    c: Coincident(g9,g8)
    c: Coincident(g9,g-15)
    c: Coincident(g10,g9)
    c: Coincident(g10,g4)
    c: Coincident(g11,g6)
    c: Coincident(g11,g-11)
    c: Coincident(g12,g11)
    c: Coincident(g12,g-11)
    c: Coincident(g13,g12)
    c: Coincident(g13,g6)
    c: Coincident(g14,g5)
    c: Coincident(g14,g-3)
    c: Coincident(g15,g14)
    c: Coincident(g15,g-3)
    c: Coincident(g16,g15)
    c: Coincident(g16,g5)
    c: Coincident(g17,g7)
    c: Coincident(g17,g-8)
    c: Coincident(g18,g17)
    c: Coincident(g18,g-8)
    c: Coincident(g19,g18)
    c: Coincident(g19,g7)
FEATURE [PartDesign::Pad] Pad007
  BaseFeature = -> Pocket016
  Direction = (1,1,1)
  Length = 9
  Length2 = 100
  Placement = pos=(0,0,0) rot=(0.57735,0.57735,0.57735;2.0944rad)
  Profile = -> Sketch048
  Type = 0
FEATURE [PartDesign::ShapeBinder] ShapeBinder013
  Support = -> [Sketch]
  TraceSupport = false
FEATURE [Sketcher::SketchObject] Sketch049
  ExternalGeometry = -> [ShapeBinder013]
  FullyConstrained = true
  MapMode = 5
  Support = -> [XY_Plane007]
  sketch-geometry (4):
    g0: LineSegment StartX=-59.3 StartY=-6.6 StartZ=0 EndX=59.3 EndY=-6.6 EndZ=0
    g1: LineSegment StartX=59.3 StartY=-6.6 StartZ=0 EndX=59.3 EndY=-73.6 EndZ=0
    g2: LineSegment StartX=59.3 StartY=-73.6 StartZ=0 EndX=-59.3 EndY=-73.6 EndZ=0
    g3: LineSegment StartX=-59.3 StartY=-73.6 StartZ=0 EndX=-59.3 EndY=-6.6 EndZ=0
  constraints (10):
    c: Coincident(g0,g1)
    c: Coincident(g1,g2)
    c: Coincident(g2,g3)
    c: Coincident(g3,g0)
    c: Horizontal(g0)
    c: Horizontal(g2)
    c: Vertical(g1)
    c: Vertical(g3)
    c: Coincident(g0,g-3)
    c: Coincident(g1,g-4)
FEATURE [PartDesign::Pad] Pad008
  Direction = (1,1,1)
  Length = 2
  Length2 = 100
  Offset = 2
  Profile = -> Sketch049
  Reversed = true
  Type = 0
FEATURE [PartDesign::ShapeBinder] ShapeBinder014
  Support = -> [Sketch031]
  TraceSupport = false
FEATURE [Sketcher::SketchObject] Sketch050
  ExternalGeometry = -> [ShapeBinder014]
  FullyConstrained = true
  MapMode = 5
  Support = -> [Pad008]
  sketch-geometry (4):
    g0: Circle CenterX=0 CenterY=-11.6 CenterZ=0 NormalX=0 NormalY=0 NormalZ=1 AngleXU=0 Radius=1.6
    g1: Circle CenterX=54.3 CenterY=-40.1 CenterZ=0 NormalX=0 NormalY=0 NormalZ=1 AngleXU=0 Radius=1.6
    g2: Circle CenterX=-54.3 CenterY=-40.1 CenterZ=0 NormalX=0 NormalY=0 NormalZ=1 AngleXU=0 Radius=1.6
    g3: Circle CenterX=0 CenterY=-68.6 CenterZ=0 NormalX=0 NormalY=0 NormalZ=1 AngleXU=0 Radius=1.6
  constraints (8):
    c: Coincident(g0,g-3)
    c: Coincident(g1,g-6)
    c: Coincident(g2,g-4)
    c: Coincident(g3,g-5)
    c: Equal(g3,g1)
    c: Equal(g1,g0)
    c: Equal(g0,g2)
    c: Radius(g3) = 1.6
FEATURE [PartDesign::Pocket] Pocket017
  BaseFeature = -> Pad008
  Length = 2
  Length2 = 100
  Profile = -> Sketch050
  Type = 0
FEATURE [PartDesign::Chamfer] Chamfer001
  Angle = 45
  Base = -> Pocket017 [Edge14,Edge15,Edge13,Edge12]
  BaseFeature = -> Pocket017
  ChamferType = 0
  FlipDirection = false
  Size = 1.6
  Size2 = 1
  SupportTransform = false
FEATURE [Sketcher::SketchObject] Sketch051
  ExternalGeometry = -> [Pad007,ShapeBinder012]
  FullyConstrained = true
  MapMode = 5
  Placement = pos=(1.4e-15,-1.3e-15,-2) rot=(0,0,-1;1.5708rad)
  Support = -> [Pad007]
  sketch-geometry (16):
    g0: LineSegment StartX=6.4 StartY=-59.5 StartZ=0 EndX=37.1 EndY=-59.5 EndZ=0
    g1: LineSegment StartX=37.1 StartY=-59.5 StartZ=0 EndX=37.1 EndY=-3 EndZ=0
    g2: LineSegment StartX=37.1 StartY=-3 StartZ=0 EndX=6.4 EndY=-3 EndZ=0
    g3: LineSegment StartX=6.4 StartY=-3 StartZ=0 EndX=6.4 EndY=-59.5 EndZ=0
    g4: LineSegment StartX=73.8 StartY=-59.5 StartZ=0 EndX=43.1 EndY=-59.5 EndZ=0
    g5: LineSegment StartX=43.1 StartY=-59.5 StartZ=0 EndX=43.1 EndY=-3 EndZ=0
    g6: LineSegment StartX=43.1 StartY=-3 StartZ=0 EndX=73.8 EndY=-3 EndZ=0
    g7: LineSegment StartX=73.8 StartY=-3 StartZ=0 EndX=73.8 EndY=-59.5 EndZ=0
    g8: LineSegment StartX=6.4 StartY=59.5 StartZ=0 EndX=37.1 EndY=59.5 EndZ=0
    g9: LineSegment StartX=37.1 StartY=59.5 StartZ=0 EndX=37.1 EndY=3 EndZ=0
    g10: LineSegment StartX=37.1 StartY=3 StartZ=0 EndX=6.4 EndY=3 EndZ=0
    g11: LineSegment StartX=6.4 StartY=3 StartZ=0 EndX=6.4 EndY=59.5 EndZ=0
    g12: LineSegment StartX=73.8 StartY=59.5 StartZ=0 EndX=43.1 EndY=59.5 EndZ=0
    g13: LineSegment StartX=43.1 StartY=59.5 StartZ=0 EndX=43.1 EndY=3 EndZ=0
    g14: LineSegment StartX=43.1 StartY=3 StartZ=0 EndX=73.8 EndY=3 EndZ=0
    g15: LineSegment StartX=73.8 StartY=3 StartZ=0 EndX=73.8 EndY=59.5 EndZ=0
  constraints (44):
    c: Coincident(g0,g1)
    c: Coincident(g1,g2)
    c: Coincident(g2,g3)
    c: Coincident(g3,g0)
    c: Horizontal(g0)
    c: Horizontal(g2)
    c: Vertical(g1)
    c: Vertical(g3)
    c: Coincident(g0,g-3)
    c: Coincident(g4,g5)
    c: Coincident(g5,g6)
    c: Coincident(g6,g7)
    c: Coincident(g7,g4)
    c: Horizontal(g4)
    c: Horizontal(g6)
    c: Vertical(g5)
    c: Vertical(g7)
    c: Coincident(g4,g-4)
    c: Coincident(g8,g9)
    c: Coincident(g9,g10)
    c: Coincident(g10,g11)
    c: Coincident(g11,g8)
    c: Horizontal(g8)
    c: Horizontal(g10)
    c: Vertical(g9)
    c: Vertical(g11)
    c: Coincident(g8,g-3)
    c: Coincident(g12,g13)
    c: Coincident(g13,g14)
    c: Coincident(g14,g15)
    c: Coincident(g15,g12)
    c: Horizontal(g12)
    c: Horizontal(g14)
    c: Vertical(g13)
    c: Vertical(g15)
    c: Coincident(g12,g-4)
    c: Vertical(g-6,g12)
    c: Horizontal(g14,g-9)
    c: Vertical(g8,g-5)
    c: Horizontal(g10,g-7)
    c: Horizontal(g2,g-8)
    c: Horizontal(g6,g-10)
    c: Vertical(g4,g-11)
    c: Vertical(g-12,g0)
FEATURE [PartDesign::Pocket] Pocket018
  BaseFeature = -> Pad007
  Length = 7.8
  Length2 = 100
  Placement = pos=(0,0,0) rot=(0.57735,0.57735,0.57735;2.0944rad)
  Profile = -> Sketch051
  Type = 0
FEATURE [Sketcher::SketchObject] Sketch052
  ExternalGeometry = -> [ShapeBinder014,Chamfer001]
  FullyConstrained = true
  MapMode = 5
  Placement = pos=(0,0,-2) rot=(1,0,0;3.14159rad)
  Support = -> [Chamfer001]
  sketch-geometry (24):
    g0: LineSegment StartX=-59.3 StartY=73.6 StartZ=0 EndX=-3.4 EndY=73.6 EndZ=0
    g1: LineSegment StartX=-3.4 StartY=73.6 StartZ=0 EndX=-3.4 EndY=71.6 EndZ=0
    g2: LineSegment StartX=-57.3 StartY=43.5 StartZ=0 EndX=-59.3 EndY=43.5 EndZ=0
    g3: LineSegment StartX=-59.3 StartY=43.5 StartZ=0 EndX=-59.3 EndY=73.6 EndZ=0
    g4: LineSegment StartX=-57.3 StartY=71.6 StartZ=0 EndX=-3.4 EndY=71.6 EndZ=0
    g5: LineSegment StartX=-57.3 StartY=43.5 StartZ=0 EndX=-57.3 EndY=71.6 EndZ=0
    g6: LineSegment StartX=59.3 StartY=73.6 StartZ=0 EndX=3.4 EndY=73.6 EndZ=0
    g7: LineSegment StartX=3.4 StartY=73.6 StartZ=0 EndX=3.4 EndY=71.6 EndZ=0
    g8: LineSegment StartX=57.3 StartY=43.5 StartZ=0 EndX=59.3 EndY=43.5 EndZ=0
    g9: LineSegment StartX=59.3 StartY=43.5 StartZ=0 EndX=59.3 EndY=73.6 EndZ=0
    g10: LineSegment StartX=57.3 StartY=43.5 StartZ=0 EndX=57.3 EndY=71.6 EndZ=0
    g11: LineSegment StartX=57.3 StartY=71.6 StartZ=0 EndX=3.4 EndY=71.6 EndZ=0
    g12: LineSegment StartX=59.3 StartY=6.6 StartZ=0 EndX=3.4 EndY=6.6 EndZ=0
    g13: LineSegment StartX=3.4 StartY=6.6 StartZ=0 EndX=3.4 EndY=8.6 EndZ=0
    g14: LineSegment StartX=57.3 StartY=36.7 StartZ=0 EndX=59.3 EndY=36.7 EndZ=0
    g15: LineSegment StartX=59.3 StartY=36.7 StartZ=0 EndX=59.3 EndY=6.6 EndZ=0
    g16: LineSegment StartX=57.3 StartY=36.7 StartZ=0 EndX=57.3 EndY=8.6 EndZ=0
    g17: LineSegment StartX=57.3 StartY=8.6 StartZ=0 EndX=3.4 EndY=8.6 EndZ=0
    g18: LineSegment StartX=-59.3 StartY=6.6 StartZ=0 EndX=-3.4 EndY=6.6 EndZ=0
    g19: LineSegment StartX=-3.4 StartY=6.6 StartZ=0 EndX=-3.4 EndY=8.6 EndZ=0
    g20: LineSegment StartX=-57.3 StartY=36.7 StartZ=0 EndX=-59.3 EndY=36.7 EndZ=0
    g21: LineSegment StartX=-59.3 StartY=36.7 StartZ=0 EndX=-59.3 EndY=6.6 EndZ=0
    g22: LineSegment StartX=-57.3 StartY=36.7 StartZ=0 EndX=-57.3 EndY=8.6 EndZ=0
    g23: LineSegment StartX=-57.3 StartY=8.6 StartZ=0 EndX=-3.4 EndY=8.6 EndZ=0
  constraints (68):
    c: Coincident(g0,g1)
    c: Coincident(g2,g3)
    c: Coincident(g3,g0)
    c: Horizontal(g0)
    c: Horizontal(g2)
    c: Vertical(g1)
    c: Vertical(g3)
    c: Coincident(g0,g-9)
    c: Coincident(g5,g4)
    c: Horizontal(g4)
    c: Vertical(g5)
    c: Coincident(g6,g7)
    c: Coincident(g8,g9)
    c: Coincident(g9,g6)
    c: Horizontal(g6)
    c: Horizontal(g8)
    c: Vertical(g7)
    c: Vertical(g9)
    c: Coincident(g6,g-9)
    c: Coincident(g10,g11)
    c: Horizontal(g11)
    c: Vertical(g10)
    c: Coincident(g12,g13)
    c: Coincident(g14,g15)
    c: Coincident(g15,g12)
    c: Horizontal(g12)
    c: Horizontal(g14)
    c: Vertical(g13)
    c: Vertical(g15)
    c: Coincident(g12,g-8)
    c: Coincident(g16,g17)
    c: Horizontal(g17)
    c: Vertical(g16)
    c: Coincident(g18,g19)
    c: Coincident(g20,g21)
    c: Coincident(g21,g18)
    c: Horizontal(g18)
    c: Horizontal(g20)
    c: Vertical(g19)
    c: Vertical(g21)
    c: Coincident(g18,g-8)
    c: Coincident(g22,g23)
    c: Horizontal(g23)
    c: Vertical(g22)
    c: Coincident(g11,g7)
    c: Coincident(g10,g8)
    c: Coincident(g16,g14)
    c: Coincident(g17,g13)
    c: Coincident(g23,g19)
    c: Coincident(g22,g20)
    c: Coincident(g5,g2)
    c: Coincident(g4,g1)
    c: Horizontal(g-5,g19)
    c: Horizontal(g-5,g13)
    c: Vertical(g20,g-7)
    c: Vertical(g-7,g2)
    c: Vertical(g-6,g8)
    c: Vertical(g-6,g14)
    c: Horizontal(g1,g-4)
    c: Horizontal(g7,g-4)
    c: DistanceX(g-4,g7) = 0.4
    c: DistanceX(g1,g-4) = 0.4
    c: DistanceY(g-7,g2) = 0.4
    c: DistanceY(g20,g-7) = 0.4
    c: DistanceY(g-6,g8) = 0.4
    c: DistanceY(g14,g-6) = 0.4
    c: DistanceX(g19,g-5) = 0.4
    c: DistanceX(g-5,g13) = 0.4
FEATURE [PartDesign::ShapeBinder] ShapeBinder015
  Support = -> [Sketch,Sketch031]
  TraceSupport = false
FEATURE [PartDesign::ShapeBinder] ShapeBinder016
  Support = -> [Sketch031]
  TraceSupport = false
FEATURE [Sketcher::SketchObject] Sketch053
  ExternalGeometry = -> [ShapeBinder016,ShapeBinder015]
  FullyConstrained = true
  MapMode = 5
  Support = -> [XY_Plane008]
  sketch-geometry (20):
    g0: LineSegment StartX=-59.3 StartY=-6.6 StartZ=0 EndX=-3.2 EndY=-6.6 EndZ=0
    g1: LineSegment StartX=59.3 StartY=-6.6 StartZ=0 EndX=59.3 EndY=-36.9 EndZ=0
    g2: LineSegment StartX=59.3 StartY=-73.6 StartZ=0 EndX=3.2 EndY=-73.6 EndZ=0
    g3: LineSegment StartX=-59.3 StartY=-73.6 StartZ=0 EndX=-59.3 EndY=-43.3 EndZ=0
    g4: LineSegment StartX=-3.2 StartY=-6.6 StartZ=0 EndX=-3.2 EndY=-11.6 EndZ=0
    g5: LineSegment StartX=3.2 StartY=-6.6 StartZ=0 EndX=3.2 EndY=-11.6 EndZ=0
    g6: LineSegment StartX=59.3 StartY=-36.9 StartZ=0 EndX=54.3 EndY=-36.9 EndZ=0
    g7: LineSegment StartX=59.3 StartY=-43.3 StartZ=0 EndX=54.3 EndY=-43.3 EndZ=0
    g8: LineSegment StartX=-59.3 StartY=-36.9 StartZ=0 EndX=-54.3 EndY=-36.9 EndZ=0
    g9: LineSegment StartX=-59.3 StartY=-43.3 StartZ=0 EndX=-54.3 EndY=-43.3 EndZ=0
    g10: LineSegment StartX=-3.2 StartY=-73.6 StartZ=0 EndX=-3.2 EndY=-68.6 EndZ=0
    g11: LineSegment StartX=3.2 StartY=-73.6 StartZ=0 EndX=3.2 EndY=-68.6 EndZ=0
    g12: LineSegment StartX=-59.3 StartY=-36.9 StartZ=0 EndX=-59.3 EndY=-6.6 EndZ=0
    g13: LineSegment StartX=3.2 StartY=-6.6 StartZ=0 EndX=59.3 EndY=-6.6 EndZ=0
    g14: LineSegment StartX=59.3 StartY=-43.3 StartZ=0 EndX=59.3 EndY=-73.6 EndZ=0
    g15: LineSegment StartX=-3.2 StartY=-73.6 StartZ=0 EndX=-59.3 EndY=-73.6 EndZ=0
    g16: ArcOfCircle CenterX=4.12844e-11 CenterY=-11.6 CenterZ=0 NormalX=0 NormalY=0 NormalZ=1 AngleXU=0 Radius=3.2 StartAngle=3.14159 EndAngle=6.28319
    g17: ArcOfCircle CenterX=54.3 CenterY=-40.1 CenterZ=0 NormalX=0 NormalY=0 NormalZ=1 AngleXU=0 Radius=3.2 StartAngle=1.5708 EndAngle=4.71239
    g18: ArcOfCircle CenterX=-4.0526e-11 CenterY=-68.6 CenterZ=0 NormalX=0 NormalY=0 NormalZ=1 AngleXU=0 Radius=3.2 StartAngle=5.36326e-11 EndAngle=3.14159
    g19: ArcOfCircle CenterX=-54.3 CenterY=-40.1 CenterZ=0 NormalX=0 NormalY=0 NormalZ=1 AngleXU=0 Radius=3.2 StartAngle=4.71239 EndAngle=7.85398
  constraints (54):
    c: Coincident(g13,g1)
    c: Coincident(g14,g2)
    c: Coincident(g15,g3)
    c: Coincident(g12,g0)
    c: Horizontal(g0)
    c: Horizontal(g2)
    c: Vertical(g1)
    c: Vertical(g3)
    c: Coincident(g0,g-11)
    c: Coincident(g14,g-12)
    c: Vertical(g4)
    c: Vertical(g5)
    c: Horizontal(g6)
    c: Horizontal(g7)
    c: Horizontal(g8)
    c: Horizontal(g9)
    c: Vertical(g10)
    c: Vertical(g11)
    c: Coincident(g12,g8)
    c: Tangent(g3,g12)
    c: Coincident(g0,g4)
    c: Coincident(g13,g5)
    c: Tangent(g0,g13)
    c: Coincident(g1,g6)
    c: Coincident(g14,g7)
    c: Tangent(g1,g14)
    c: Coincident(g2,g11)
    c: Coincident(g15,g10)
    c: Tangent(g2,g15)
    c: Coincident(g3,g9)
    c: DistanceX(g10,g-7) = 0.2
    c: Vertical(g6,g-5)
    c: Vertical(g-5,g7)
    c: Horizontal(g11,g-6)
    c: Horizontal(g-6,g10)
    c: Vertical(g9,g-8)
    c: Vertical(g-8,g8)
    c: Horizontal(g4,g-4)
    c: Horizontal(g-4,g5)
    c: DistanceX(g4,g-4) = 0.2
    c: DistanceY(g7,g-10) = 0.2
    c: DistanceY(g-3,g8) = 0.2
    c: Coincident(g16,g-9)
    c: Coincident(g16,g5)
    c: Coincident(g16,g4)
    c: Coincident(g17,g-10)
    c: Coincident(g17,g6)
    c: Coincident(g17,g7)
    c: Coincident(g18,g-7)
    c: Coincident(g18,g10)
    c: Coincident(g18,g11)
    c: Coincident(g19,g-8)
    c: Coincident(g19,g9)
    c: Coincident(g19,g8)
FEATURE [PartDesign::Pad] Pad010
  Direction = (1,1,1)
  Length = 1.6
  Length2 = 100
  Profile = -> Sketch053
  Type = 0
FEATURE [TechDraw::DrawSVGTemplate] Template001
  EditableTexts = Designed_by_Name=<owner>; Drawing_number=1; FC-Date=2023/02/27; FC-SC=1:1; FC-SH=1; FC-Title=Title; Subtitle=PCB Outline; Weight=n/a
  Height = 210
  Orientation = 1
  Width = 297
FEATURE [PartDesign::ShapeBinder] ShapeBinder017
  Support = -> [Sketch032]
  TraceSupport = false
FEATURE [Sketcher::SketchObject] Sketch055
  ExternalGeometry = -> [ShapeBinder017]
  FullyConstrained = true
  MapMode = 5
  Placement = pos=(0,0,1.6) rot=(0,0,1;0rad)
  Support = -> [Pad010]
  sketch-geometry (12):
    g0: LineSegment StartX=6.9 StartY=-59.2 StartZ=0 EndX=22.3 EndY=-59.2 EndZ=0
    g1: LineSegment StartX=22.3 StartY=-59.2 StartZ=0 EndX=22.3 EndY=-71.2 EndZ=0
    g2: LineSegment StartX=22.3 StartY=-71.2 StartZ=0 EndX=6.9 EndY=-71.2 EndZ=0
    g3: LineSegment StartX=6.9 StartY=-71.2 StartZ=0 EndX=6.9 EndY=-59.2 EndZ=0
    g4: LineSegment StartX=43.9 StartY=-8.5 StartZ=0 EndX=58.9 EndY=-8.5 EndZ=0
    g5: LineSegment StartX=58.9 StartY=-8.5 StartZ=0 EndX=58.9 EndY=-32 EndZ=0
    g6: LineSegment StartX=58.9 StartY=-32 StartZ=0 EndX=43.9 EndY=-32 EndZ=0
    g7: LineSegment StartX=43.9 StartY=-32 StartZ=0 EndX=43.9 EndY=-8.5 EndZ=0
    g8: LineSegment StartX=24.3 StartY=-47.2 StartZ=0 EndX=58.3 EndY=-47.2 EndZ=0
    g9: LineSegment StartX=58.3 StartY=-47.2 StartZ=0 EndX=58.3 EndY=-72.6 EndZ=0
    g10: LineSegment StartX=58.3 StartY=-72.6 StartZ=0 EndX=24.3 EndY=-72.6 EndZ=0
    g11: LineSegment StartX=24.3 StartY=-72.6 StartZ=0 EndX=24.3 EndY=-47.2 EndZ=0
  constraints (30):
    c: Coincident(g0,g1)
    c: Coincident(g1,g2)
    c: Coincident(g2,g3)
    c: Coincident(g3,g0)
    c: Horizontal(g0)
    c: Horizontal(g2)
    c: Vertical(g1)
    c: Vertical(g3)
    c: Coincident(g4,g5)
    c: Coincident(g5,g6)
    c: Coincident(g6,g7)
    c: Coincident(g7,g4)
    c: Horizontal(g4)
    c: Horizontal(g6)
    c: Vertical(g5)
    c: Vertical(g7)
    c: Coincident(g4,g-7)
    c: Coincident(g5,g-8)
    c: Coincident(g8,g9)
    c: Coincident(g9,g10)
    c: Coincident(g10,g11)
    c: Coincident(g11,g8)
    c: Horizontal(g8)
    c: Horizontal(g10)
    c: Vertical(g9)
    c: Vertical(g11)
    c: Coincident(g8,g-5)
    c: Coincident(g9,g-6)
    c: Coincident(g-4,g1)
    c: Coincident(g-3,g0)
FEATURE [PartDesign::Pad] Pad011
  BaseFeature = -> Pad010
  Direction = (1,1,1)
  Length = 1.6
  Length2 = 100
  Profile = -> Sketch055
  Type = 0
FEATURE [Sketcher::SketchObject] Sketch056
  ExternalGeometry = -> [ShapeBinder017]
  FullyConstrained = true
  MapMode = 5
  Placement = pos=(0,0,1.6) rot=(0,0,1;0rad)
  Support = -> [Pad011]
  sketch-geometry (4):
    g0: LineSegment StartX=-58.1 StartY=-46.6 StartZ=0 EndX=-32.1 EndY=-46.6 EndZ=0
    g1: LineSegment StartX=-32.1 StartY=-46.6 StartZ=0 EndX=-32.1 EndY=-72.6 EndZ=0
    g2: LineSegment StartX=-32.1 StartY=-72.6 StartZ=0 EndX=-58.1 EndY=-72.6 EndZ=0
    g3: LineSegment StartX=-58.1 StartY=-72.6 StartZ=0 EndX=-58.1 EndY=-46.6 EndZ=0
  constraints (10):
    c: Coincident(g0,g1)
    c: Coincident(g1,g2)
    c: Coincident(g2,g3)
    c: Coincident(g3,g0)
    c: Horizontal(g0)
    c: Horizontal(g2)
    c: Vertical(g1)
    c: Vertical(g3)
    c: Coincident(g0,g-3)
    c: Coincident(g1,g-4)
FEATURE [PartDesign::Pad] Pad012
  BaseFeature = -> Pad011
  Direction = (1,1,1)
  Length = 5.8
  Length2 = 100
  Profile = -> Sketch056
  Type = 0
FEATURE [Sketcher::SketchObject] Sketch057
  ExternalGeometry = -> [ShapeBinder017]
  FullyConstrained = true
  MapMode = 5
  Placement = pos=(0,0,1.6) rot=(0,0,1;0rad)
  Support = -> [Pad012]
  sketch-geometry (4):
    g0: LineSegment StartX=-56.3 StartY=-9.4 StartZ=0 EndX=-36.3 EndY=-9.4 EndZ=0
    g1: LineSegment StartX=-36.3 StartY=-9.4 StartZ=0 EndX=-36.3 EndY=-23.4 EndZ=0
    g2: LineSegment StartX=-36.3 StartY=-23.4 StartZ=0 EndX=-56.3 EndY=-23.4 EndZ=0
    g3: LineSegment StartX=-56.3 StartY=-23.4 StartZ=0 EndX=-56.3 EndY=-9.4 EndZ=0
  constraints (10):
    c: Coincident(g0,g1)
    c: Coincident(g1,g2)
    c: Coincident(g2,g3)
    c: Coincident(g3,g0)
    c: Horizontal(g0)
    c: Horizontal(g2)
    c: Vertical(g1)
    c: Vertical(g3)
    c: Coincident(g0,g-3)
    c: Coincident(g1,g-4)
FEATURE [PartDesign::Pad] Pad013
  BaseFeature = -> Pad012
  Direction = (1,1,1)
  Length = 4
  Length2 = 100
  Profile = -> Sketch057
  Type = 0
FEATURE [Sketcher::SketchObject] Sketch058
  ExternalGeometry = -> [ShapeBinder017]
  FullyConstrained = true
  MapMode = 5
  Placement = pos=(0,0,1.6) rot=(0,0,1;0rad)
  Support = -> [Pad013]
  sketch-geometry (4):
    g0: LineSegment StartX=21.9 StartY=-10.6 StartZ=0 EndX=34.3 EndY=-10.6 EndZ=0
    g1: LineSegment StartX=34.3 StartY=-10.6 StartZ=0 EndX=34.3 EndY=-18.6 EndZ=0
    g2: LineSegment StartX=34.3 StartY=-18.6 StartZ=0 EndX=21.9 EndY=-18.6 EndZ=0
    g3: LineSegment StartX=21.9 StartY=-18.6 StartZ=0 EndX=21.9 EndY=-10.6 EndZ=0
  constraints (10):
    c: Coincident(g0,g1)
    c: Coincident(g1,g2)
    c: Coincident(g2,g3)
    c: Coincident(g3,g0)
    c: Horizontal(g0)
    c: Horizontal(g2)
    c: Vertical(g1)
    c: Vertical(g3)
    c: Coincident(g0,g-3)
    c: Coincident(g1,g-4)
FEATURE [PartDesign::Pad] Pad014
  BaseFeature = -> Pad013
  Direction = (1,1,1)
  Length = 5
  Length2 = 100
  Profile = -> Sketch058
  Type = 0
FEATURE [Sketcher::SketchObject] Sketch059
  ExternalGeometry = -> [Pad014]
  FullyConstrained = true
  MapMode = 5
  Placement = pos=(0,0,3.2) rot=(0,0,1;0rad)
  Support = -> [Pad014]
  sketch-geometry (4):
    g0: LineSegment StartX=58.3 StartY=-55.2 StartZ=0 EndX=50.9 EndY=-55.2 EndZ=0
    g1: LineSegment StartX=50.9 StartY=-55.2 StartZ=0 EndX=50.9 EndY=-64.2 EndZ=0
    g2: LineSegment StartX=50.9 StartY=-64.2 StartZ=0 EndX=58.3 EndY=-64.2 EndZ=0
    g3: LineSegment StartX=58.3 StartY=-64.2 StartZ=0 EndX=58.3 EndY=-55.2 EndZ=0
  constraints (12):
    c: Coincident(g0,g1)
    c: Coincident(g1,g2)
    c: Coincident(g2,g3)
    c: Coincident(g3,g0)
    c: Horizontal(g0)
    c: Horizontal(g2)
    c: Vertical(g1)
    c: Vertical(g3)
    c: PointOnObject(g0,g-3)
    c: DistanceX(g2,g2) = 7.4
    c: DistanceY(g1,g1) = 9
    c: DistanceY(g0,g-3) = 8
FEATURE [PartDesign::Pad] Pad015
  BaseFeature = -> Pad014
  Direction = (1,1,1)
  Length = 3
  Length2 = 100
  Profile = -> Sketch059
  Type = 0
FEATURE [Sketcher::SketchObject] Sketch060
  ExternalGeometry = -> [ShapeBinder017]
  FullyConstrained = true
  MapMode = 5
  Placement = pos=(0,0,1.6) rot=(0,0,1;0rad)
  Support = -> [Pad015]
  sketch-geometry (16):
    g0: LineSegment StartX=-14.9 StartY=-35.6 StartZ=0 EndX=-10.5 EndY=-35.6 EndZ=0
    g1: LineSegment StartX=-10.5 StartY=-35.6 StartZ=0 EndX=-10.5 EndY=-40 EndZ=0
    g2: LineSegment StartX=-10.5 StartY=-40 StartZ=0 EndX=-14.9 EndY=-40 EndZ=0
    g3: LineSegment StartX=-14.9 StartY=-40 StartZ=0 EndX=-14.9 EndY=-35.6 EndZ=0
    g4: LineSegment StartX=-2.2 StartY=-22.9 StartZ=0 EndX=2.2 EndY=-22.9 EndZ=0
    g5: LineSegment StartX=2.2 StartY=-22.9 StartZ=0 EndX=2.2 EndY=-27.3 EndZ=0
    g6: LineSegment StartX=2.2 StartY=-27.3 StartZ=0 EndX=-2.2 EndY=-27.3 EndZ=0
    g7: LineSegment StartX=-2.2 StartY=-27.3 StartZ=0 EndX=-2.2 EndY=-22.9 EndZ=0
    g8: LineSegment StartX=10.5 StartY=-35.6 StartZ=0 EndX=14.9 EndY=-35.6 EndZ=0
    g9: LineSegment StartX=14.9 StartY=-35.6 StartZ=0 EndX=14.9 EndY=-40 EndZ=0
    g10: LineSegment StartX=14.9 StartY=-40 StartZ=0 EndX=10.5 EndY=-40 EndZ=0
    g11: LineSegment StartX=10.5 StartY=-40 StartZ=0 EndX=10.5 EndY=-35.6 EndZ=0
    g12: LineSegment StartX=-2.2 StartY=-48.7 StartZ=0 EndX=2.2 EndY=-48.7 EndZ=0
    g13: LineSegment StartX=2.2 StartY=-48.7 StartZ=0 EndX=2.2 EndY=-53.1 EndZ=0
    g14: LineSegment StartX=2.2 StartY=-53.1 StartZ=0 EndX=-2.2 EndY=-53.1 EndZ=0
    g15: LineSegment StartX=-2.2 StartY=-53.1 StartZ=0 EndX=-2.2 EndY=-48.7 EndZ=0
  constraints (40):
    c: Coincident(g0,g1)
    c: Coincident(g1,g2)
    c: Coincident(g2,g3)
    c: Coincident(g3,g0)
    c: Horizontal(g0)
    c: Horizontal(g2)
    c: Vertical(g1)
    c: Vertical(g3)
    c: Coincident(g0,g-3)
    c: Coincident(g1,g-4)
    c: Coincident(g4,g5)
    c: Coincident(g5,g6)
    c: Coincident(g6,g7)
    c: Coincident(g7,g4)
    c: Horizontal(g4)
    c: Horizontal(g6)
    c: Vertical(g5)
    c: Vertical(g7)
    c: Coincident(g4,g-5)
    c: Coincident(g5,g-6)
    c: Coincident(g8,g9)
    c: Coincident(g9,g10)
    c: Coincident(g10,g11)
    c: Coincident(g11,g8)
    c: Horizontal(g8)
    c: Horizontal(g10)
    c: Vertical(g9)
    c: Vertical(g11)
    c: Coincident(g8,g-9)
    c: Coincident(g9,g-10)
    c: Coincident(g12,g13)
    c: Coincident(g13,g14)
    c: Coincident(g14,g15)
    c: Coincident(g15,g12)
    c: Horizontal(g12)
    c: Horizontal(g14)
    c: Vertical(g13)
    c: Vertical(g15)
    c: Coincident(g12,g-7)
    c: Coincident(g13,g-8)
FEATURE [PartDesign::Pad] Pad016
  BaseFeature = -> Pad015
  Direction = (1,1,1)
  Length = 3
  Length2 = 100
  Profile = -> Sketch060
  Type = 0
FEATURE [Sketcher::SketchObject] Sketch061
  ExternalGeometry = -> [Pad016]
  FullyConstrained = true
  MapMode = 5
  Placement = pos=(0,0,4.6) rot=(0,0,1;0rad)
  Support = -> [Pad016]
  sketch-geometry (4):
    g0: Circle CenterX=-12.7 CenterY=-37.8 CenterZ=0 NormalX=0 NormalY=0 NormalZ=1 AngleXU=0 Radius=1.2
    g1: Circle CenterX=-1e-16 CenterY=-25.1 CenterZ=0 NormalX=0 NormalY=0 NormalZ=1 AngleXU=0 Radius=1.2
    g2: Circle CenterX=12.7 CenterY=-37.8 CenterZ=0 NormalX=0 NormalY=0 NormalZ=1 AngleXU=0 Radius=1.2
    g3: Circle CenterX=-1e-16 CenterY=-50.9 CenterZ=0 NormalX=0 NormalY=0 NormalZ=1 AngleXU=0 Radius=1.2
  constraints (12):
    c: Equal(g3,g2)
    c: Equal(g2,g1)
    c: Equal(g1,g0)
    c: Radius(g2) = 1.2
    c: Horizontal(g0,g2)
    c: Vertical(g3,g1)
    c: DistanceX(g-5,g1) = 2.2
    c: DistanceY(g2,g-7) = 2.2
    c: DistanceX(g2,g-7) = 2.2
    c: DistanceX(g-3,g0) = 2.2
    c: DistanceY(g-10,g3) = 2.2
    c: DistanceY(g-6,g1) = 2.2
FEATURE [PartDesign::Pad] Pad017
  BaseFeature = -> Pad016
  Direction = (1,1,1)
  Length = 2
  Length2 = 100
  Profile = -> Sketch061
  Type = 0
FEATURE [PartDesign::Body] Body008  label="Main PCB"
  Group = -> [ShapeBinder015,ShapeBinder016,ShapeBinder017,Sketch053,Pad010,Sketch055,Pad011,Sketch056,Pad012,Sketch057,Pad013,Sketch058,Pad014,Sketch059,Pad015,Sketch060,Pad016,Sketch061,Pad017]
  Origin = -> Origin008
  Placement = pos=(0,0,-9.8) rot=(0,0,1;0rad)
  Tip = -> Pad017
FEATURE [TechDraw::DrawViewPart] View004  label="PCB outline"
  CoarseView = false
  Direction = (0,0,1)
  Focus = 100
  HardHidden = false
  IsoCount = 0
  IsoHidden = false
  IsoVisible = false
  LockPosition = false
  Perspective = false
  Rotation = 0
  ScaleType = 0
  SeamHidden = false
  SeamVisible = true
  SmoothHidden = false
  SmoothVisible = true
  Source = -> [Body008]
  X = 148.5
  XDirection = (1,0,0)
  Y = 121.501
FEATURE [TechDraw::DrawViewDimension] Dimension
  Arbitrary = false
  ArbitraryTolerances = false
  EqualTolerance = true
  FormatSpec = %.2f
  FormatSpecOverTolerance = %+.2f
  FormatSpecUnderTolerance = %+.2f
  Inverted = false
  LockPosition = false
  MeasureType = 1
  OverTolerance = 0
  References2D = -> [View004]
  Rotation = 0
  ScaleType = 0
  TheoreticalExact = false
  Type = 1
  UnderTolerance = 0
  X = 3.33089
  Y = 60.1471
FEATURE [TechDraw::DrawViewDimension] Dimension001
  Arbitrary = false
  ArbitraryTolerances = false
  EqualTolerance = true
  FormatSpec = %.2f
  FormatSpecOverTolerance = %+.2f
  FormatSpecUnderTolerance = %+.2f
  Inverted = false
  LockPosition = false
  MeasureType = 1
  OverTolerance = 0
  References2D = -> [View004]
  Rotation = 0
  ScaleType = 0
  TheoreticalExact = false
  Type = 1
  UnderTolerance = 0
  X = -32.0187
  Y = 51.6918
FEATURE [TechDraw::DrawViewDimension] Dimension004
  Arbitrary = false
  ArbitraryTolerances = false
  EqualTolerance = true
  FormatSpec = %.2f
  FormatSpecOverTolerance = %+.2f
  FormatSpecUnderTolerance = %+.2f
  Inverted = false
  LockPosition = false
  MeasureType = 1
  OverTolerance = 0
  References2D = -> [View004]
  Rotation = 0
  ScaleType = 0
  TheoreticalExact = false
  Type = 2
  UnderTolerance = 0
  X = -84.1536
  Y = -14.3485
FEATURE [TechDraw::DrawViewDimension] Dimension005
  Arbitrary = false
  ArbitraryTolerances = false
  EqualTolerance = true
  FormatSpec = %.2f
  FormatSpecOverTolerance = %+.2f
  FormatSpecUnderTolerance = %+.2f
  Inverted = false
  LockPosition = false
  MeasureType = 1
  OverTolerance = 0
  References2D = -> [View004]
  Rotation = 0
  ScaleType = 0
  TheoreticalExact = false
  Type = 2
  UnderTolerance = 0
  X = -72.8798
  Y = -14.5067
FEATURE [TechDraw::DrawViewDimension] Dimension006
  Arbitrary = false
  ArbitraryTolerances = false
  EqualTolerance = true
  FormatSpec = %.2f
  FormatSpecOverTolerance = %+.2f
  FormatSpecUnderTolerance = %+.2f
  Inverted = false
  LockPosition = false
  MeasureType = 1
  OverTolerance = 0
  References2D = -> [View004]
  Rotation = 0
  ScaleType = 0
  TheoreticalExact = false
  Type = 1
  UnderTolerance = 0
  X = -40.6248
  Y = 14.637
FEATURE [TechDraw::DrawViewDimension] Dimension007
  Arbitrary = false
  ArbitraryTolerances = false
  EqualTolerance = true
  FormatSpec = R%.2f
  FormatSpecOverTolerance = %+.2f
  FormatSpecUnderTolerance = %+.2f
  Inverted = false
  LockPosition = false
  MeasureType = 1
  OverTolerance = 0
  References2D = -> [View004]
  Rotation = 0
  ScaleType = 0
  TheoreticalExact = false
  Type = 4
  UnderTolerance = 0
  X = -39.0774
  Y = -3.87791
FEATURE [TechDraw::DrawPage] Page001  label="Page-Main PCB"
  KeepUpdated = true
  NextBalloonIndex = 1
  ProjectionType = 0
  Template = -> Template001
  Views = -> [View004,Dimension,Dimension001,Dimension004,Dimension005,Dimension006,Dimension007]
FEATURE [Sketcher::SketchObject] Sketch062
  FullyConstrained = true
  MapMode = 5
  Placement = pos=(-31.5,6.9e-15,-1.92e-14) rot=(0.57735,0.57735,-0.57735;4.18879rad)
  Support = -> [Chamfer]
  sketch-geometry (1):
    g0: Circle CenterX=0 CenterY=0 CenterZ=0 NormalX=0 NormalY=0 NormalZ=1 AngleXU=0 Radius=1.8
  constraints (2):
    c: Coincident(g0,g-1)
    c: Radius(g0) = 1.8
FEATURE [PartDesign::Pocket] Pocket020
  BaseFeature = -> Chamfer
  Length = 20
  Length2 = 100
  Placement = pos=(0,0,0) rot=(0.57735,0.57735,0.57735;2.0944rad)
  Profile = -> Sketch062
  Type = 0
FEATURE [PartDesign::ShapeBinder] ShapeBinder018
  Support = -> [Sketch032]
  TraceSupport = false
FEATURE [Sketcher::SketchObject] Sketch063
  ExternalGeometry = -> [ShapeBinder018]
  FullyConstrained = true
  MapMode = 5
  Placement = pos=(-1.9e-15,-4.4,2.1e-15) rot=(0.57735,0.57735,0.57735;4.18879rad)
  Support = -> [Pocket018]
  sketch-geometry (4):
    g0: LineSegment StartX=-8.3 StartY=35.3 StartZ=0 EndX=-2.3 EndY=35.3 EndZ=0
    g1: LineSegment StartX=-2.3 StartY=35.3 StartZ=0 EndX=-2.3 EndY=20.9 EndZ=0
    g2: LineSegment StartX=-2.3 StartY=20.9 StartZ=0 EndX=-8.3 EndY=20.9 EndZ=0
    g3: LineSegment StartX=-8.3 StartY=20.9 StartZ=0 EndX=-8.3 EndY=35.3 EndZ=0
  constraints (12):
    c: Coincident(g0,g1)
    c: Coincident(g1,g2)
    c: Coincident(g2,g3)
    c: Coincident(g3,g0)
    c: Horizontal(g0)
    c: Horizontal(g2)
    c: Vertical(g1)
    c: Vertical(g3)
    c: DistanceX(g2,g2) = 6
    c: DistanceY(g-3,g0) = 1
    c: DistanceY(g1,g-3) = 1
    c: DistanceX(g1,g-3) = 2.3
FEATURE [PartDesign::Pocket] Pocket021
  BaseFeature = -> Pocket018
  Length = 3
  Length2 = 100
  Placement = pos=(0,0,0) rot=(0.57735,0.57735,0.57735;2.0944rad)
  Profile = -> Sketch063
  Type = 0
FEATURE [Sketcher::SketchObject] Sketch064
  ExternalGeometry = -> [ShapeBinder018]
  FullyConstrained = true
  MapMode = 5
  Placement = pos=(61.5,-1.35e-14,1.35e-14) rot=(0.57735,0.57735,0.57735;2.0944rad)
  Support = -> [Pocket021]
  sketch-geometry (4):
    g0: LineSegment StartX=-67.2 StartY=-2 StartZ=0 EndX=-53.2 EndY=-2 EndZ=0
    g1: LineSegment StartX=-53.2 StartY=-2 StartZ=0 EndX=-53.2 EndY=-8 EndZ=0
    g2: LineSegment StartX=-53.2 StartY=-8 StartZ=0 EndX=-67.2 EndY=-8 EndZ=0
    g3: LineSegment StartX=-67.2 StartY=-8 StartZ=0 EndX=-67.2 EndY=-2 EndZ=0
  constraints (12):
    c: Coincident(g0,g1)
    c: Coincident(g1,g2)
    c: Coincident(g2,g3)
    c: Coincident(g3,g0)
    c: Horizontal(g0)
    c: Horizontal(g2)
    c: Vertical(g1)
    c: Vertical(g3)
    c: DistanceX(g2,g2) = 14
    c: DistanceY(g3,g3) = 6
    c: DistanceX(g0,g-3) = 6
    c: DistanceY(g0,g-3) = 2
FEATURE [PartDesign::Pocket] Pocket022
  BaseFeature = -> Pocket021
  Length = 3
  Length2 = 100
  Placement = pos=(0,0,0) rot=(0.57735,0.57735,0.57735;2.0944rad)
  Profile = -> Sketch064
  Type = 0
FEATURE [PartDesign::Pad] Pad018
  BaseFeature = -> Chamfer001
  Direction = (1,1,1)
  Length = 0.4
  Length2 = 100
  Profile = -> Sketch052
  Type = 0
FEATURE [PartDesign::ShapeBinder] ShapeBinder019
  Support = -> [Sketch032]
  TraceSupport = false
FEATURE [Sketcher::SketchObject] Sketch065
  ExternalGeometry = -> [ShapeBinder019]
  FullyConstrained = true
  MapMode = 5
  Support = -> [Pad018]
  sketch-geometry (32):
    g0: ArcOfCircle CenterX=-48.8 CenterY=-12.4 CenterZ=0 NormalX=0 NormalY=0 NormalZ=1 AngleXU=0 Radius=1 StartAngle=1.5708 EndAngle=4.71239
    g1: ArcOfCircle CenterX=-43.8 CenterY=-12.4 CenterZ=0 NormalX=0 NormalY=0 NormalZ=1 AngleXU=0 Radius=1 StartAngle=4.71239 EndAngle=7.85398
    g2: LineSegment StartX=-48.8 StartY=-13.4 StartZ=0 EndX=-43.8 EndY=-13.4 EndZ=0
    g3: LineSegment StartX=-48.8 StartY=-11.4 StartZ=0 EndX=-43.8 EndY=-11.4 EndZ=0
    g4: ArcOfCircle CenterX=-52.3 CenterY=-16.4 CenterZ=0 NormalX=0 NormalY=0 NormalZ=1 AngleXU=0 Radius=1 StartAngle=1.5708 EndAngle=4.71239
    g5: ArcOfCircle CenterX=-40.3 CenterY=-16.4 CenterZ=0 NormalX=0 NormalY=0 NormalZ=1 AngleXU=0 Radius=1 StartAngle=4.71239 EndAngle=7.85398
    g6: LineSegment StartX=-52.3 StartY=-17.4 StartZ=0 EndX=-40.3 EndY=-17.4 EndZ=0
    g7: LineSegment StartX=-52.3 StartY=-15.4 StartZ=0 EndX=-40.3 EndY=-15.4 EndZ=0
    g8: ArcOfCircle CenterX=-48.8 CenterY=-20.4 CenterZ=0 NormalX=0 NormalY=0 NormalZ=1 AngleXU=0 Radius=1 StartAngle=1.5708 EndAngle=4.71239
    g9: ArcOfCircle CenterX=-43.8 CenterY=-20.4 CenterZ=0 NormalX=0 NormalY=0 NormalZ=1 AngleXU=0 Radius=1 StartAngle=4.71239 EndAngle=7.85398
    g10: LineSegment StartX=-48.8 StartY=-21.4 StartZ=0 EndX=-43.8 EndY=-21.4 EndZ=0
    g11: LineSegment StartX=-48.8 StartY=-19.4 StartZ=0 EndX=-43.8 EndY=-19.4 EndZ=0
    g12: LineSegment StartX=-17.7 StartY=-32.8 StartZ=0 EndX=-7.7 EndY=-32.8 EndZ=0
    g13: LineSegment StartX=-7.7 StartY=-42.8 StartZ=0 EndX=-17.7 EndY=-42.8 EndZ=0
    g14: LineSegment StartX=-17.7 StartY=-42.8 StartZ=0 EndX=-17.7 EndY=-32.8 EndZ=0
    g15: LineSegment StartX=-5 StartY=-20.1 StartZ=0 EndX=5 EndY=-20.1 EndZ=0
    g16: LineSegment StartX=5 StartY=-20.1 StartZ=0 EndX=5 EndY=-30.1 EndZ=0
    g17: LineSegment StartX=-5 StartY=-30.1 StartZ=0 EndX=-5 EndY=-20.1 EndZ=0
    g18: LineSegment StartX=7.7 StartY=-32.8 StartZ=0 EndX=17.7 EndY=-32.8 EndZ=0
    g19: LineSegment StartX=17.7 StartY=-32.8 StartZ=0 EndX=17.7 EndY=-42.8 EndZ=0
    g20: LineSegment StartX=17.7 StartY=-42.8 StartZ=0 EndX=7.7 EndY=-42.8 EndZ=0
    g21: LineSegment StartX=5 StartY=-45.9 StartZ=0 EndX=5 EndY=-55.9 EndZ=0
    g22: LineSegment StartX=5 StartY=-55.9 StartZ=0 EndX=-5 EndY=-55.9 EndZ=0
    g23: LineSegment StartX=-5 StartY=-55.9 StartZ=0 EndX=-5 EndY=-45.9 EndZ=0
    g24: LineSegment StartX=-7.7 StartY=-32.8 StartZ=0 EndX=-2.7 EndY=-37.8 EndZ=0
    g25: LineSegment StartX=-7.7 StartY=-42.8 StartZ=0 EndX=-2.7 EndY=-37.8 EndZ=0
    g26: LineSegment StartX=-5 StartY=-30.1 StartZ=0 EndX=0 EndY=-35.1 EndZ=0
    g27: LineSegment StartX=0 StartY=-35.1 StartZ=0 EndX=5 EndY=-30.1 EndZ=0
    g28: LineSegment StartX=7.7 StartY=-32.8 StartZ=0 EndX=2.7 EndY=-37.8 EndZ=0
    g29: LineSegment StartX=7.7 StartY=-42.8 StartZ=0 EndX=2.7 EndY=-37.8 EndZ=0
    g30: LineSegment StartX=-5 StartY=-45.9 StartZ=0 EndX=0 EndY=-40.9 EndZ=0
    g31: LineSegment StartX=5 StartY=-45.9 StartZ=0 EndX=0 EndY=-40.9 EndZ=0
  constraints (90):
    c: Tangent(g0,g3) = 1.5708
    c: Tangent(g0,g2) = -1.5708
    c: Tangent(g2,g1) = -1.5708
    c: Tangent(g3,g1) = 1.5708
    c: Horizontal(g2)
    c: Equal(g0,g1)
    c: Tangent(g4,g7) = 1.5708
    c: Tangent(g4,g6) = -1.5708
    c: Tangent(g6,g5) = -1.5708
    c: Tangent(g7,g5) = 1.5708
    c: Horizontal(g6)
    c: Equal(g4,g5)
    c: Tangent(g8,g11) = 1.5708
    c: Tangent(g8,g10) = -1.5708
    c: Tangent(g10,g9) = -1.5708
    c: Tangent(g11,g9) = 1.5708
    c: Horizontal(g10)
    c: Equal(g8,g9)
    c: Coincident(g13,g14)
    c: Coincident(g14,g12)
    c: Horizontal(g12)
    c: Horizontal(g13)
    c: Vertical(g14)
    c: Coincident(g15,g16)
    c: Coincident(g17,g15)
    c: Horizontal(g15)
    c: Vertical(g16)
    c: Vertical(g17)
    c: Coincident(g18,g19)
    c: Coincident(g19,g20)
    c: Horizontal(g18)
    c: Horizontal(g20)
    c: Vertical(g19)
    c: Coincident(g21,g22)
    c: Coincident(g22,g23)
    c: Horizontal(g22)
    c: Vertical(g21)
    c: Vertical(g23)
    c: Coincident(g24,g12)
    c: Coincident(g25,g24)
    c: Coincident(g27,g26)
    c: Coincident(g27,g16)
    c: Coincident(g28,g18)
    c: Coincident(g29,g20)
    c: Coincident(g29,g28)
    c: Coincident(g31,g30)
    c: Equal(g4,g0)
    c: Equal(g0,g8)
    c: Radius(g1) = 1
    c: Equal(g11,g2)
    c: DistanceY(g9,g5) = 2
    c: DistanceY(g5,g1) = 2
    c: DistanceX(g3,g3) = 5
    c: DistanceX(g7,g7) = 12
    c: DistanceY(g-4,g9) = 2
    c: DistanceX(g-3,g4) = 4
    c: DistanceX(g-3,g0) = 7.5
    c: Vertical(g8,g0)
    c: Equal(g12,g14)
    c: Equal(g14,g23)
    c: Equal(g23,g22)
    c: Equal(g22,g20)
    c: Equal(g20,g19)
    c: Equal(g19,g16)
    c: Equal(g16,g15)
    c: PointOnObject(g26,g-2)
    c: PointOnObject(g30,g-2)
    c: Coincident(g30,g23)
    c: Coincident(g21,g31)
    c: Coincident(g17,g26)
    c: Equal(g26,g27)
    c: Equal(g27,g28)
    c: Equal(g28,g29)
    c: Equal(g29,g31)
    c: Equal(g31,g30)
    c: Equal(g30,g25)
    c: Equal(g25,g24)
    c: Coincident(g13,g25)
    c: Vertical(g12,g13)
    c: Vertical(g18,g20)
    c: Horizontal(g17,g16)
    c: Horizontal(g23,g21)
    c: DistanceY(g19,g19) = 10
    c: Horizontal(g12,g18)
    c: DistanceY(g-8,g18) = 2.8
    c: DistanceX(g-8,g18) = 2.8
    c: DistanceY(g21,g-7) = 2.8
    c: DistanceX(g13,g-5) = 2.8
    c: Angle(g25) = 0.785398
    c: DistanceY(g-6,g15) = 2.8
FEATURE [PartDesign::Pocket] Pocket023
  BaseFeature = -> Pad018
  Length = 5
  Length2 = 100
  Profile = -> Sketch065
  Type = 1
FEATURE [PartDesign::Body] Body007  label="Main Cover"
  Group = -> [ShapeBinder013,ShapeBinder014,Sketch049,Pad008,Sketch050,Pocket017,Chamfer001,Sketch052,Pad018,ShapeBinder019,Sketch065,Pocket023]
  Origin = -> Origin007
  Tip = -> Pocket023
FEATURE [PartDesign::ShapeBinder] ShapeBinder020
  Support = -> [Sketch032]
  TraceSupport = false
FEATURE [Sketcher::SketchObject] Sketch066
  ExternalGeometry = -> [ShapeBinder020]
  FullyConstrained = true
  MapMode = 5
  Support = -> [XY_Plane010]
  sketch-geometry (4):
    g0: LineSegment StartX=5.7 StartY=-58 StartZ=0 EndX=23.5 EndY=-58 EndZ=0
    g1: LineSegment StartX=23.5 StartY=-58 StartZ=0 EndX=23.5 EndY=-72.4 EndZ=0
    g2: LineSegment StartX=23.5 StartY=-72.4 StartZ=0 EndX=5.7 EndY=-72.4 EndZ=0
    g3: LineSegment StartX=5.7 StartY=-72.4 StartZ=0 EndX=5.7 EndY=-58 EndZ=0
  constraints (12):
    c: Coincident(g0,g1)
    c: Coincident(g1,g2)
    c: Coincident(g2,g3)
    c: Coincident(g3,g0)
    c: Horizontal(g0)
    c: Horizontal(g2)
    c: Vertical(g1)
    c: Vertical(g3)
    c: DistanceX(g0,g-3) = 1.2
    c: DistanceY(g-3,g0) = 1.2
    c: DistanceX(g-4,g1) = 1.2
    c: DistanceY(g1,g-4) = 1.2
FEATURE [PartDesign::Pad] Pad019
  Direction = (1,1,1)
  Length = 5.6
  Length2 = 100
  Profile = -> Sketch066
  Type = 0
FEATURE [Sketcher::SketchObject] Sketch067
  ExternalGeometry = -> [ShapeBinder020]
  FullyConstrained = true
  MapMode = 5
  Placement = pos=(0,0,0) rot=(1,0,0;3.14159rad)
  Support = -> [Pad019]
  sketch-geometry (4):
    g0: LineSegment StartX=6.7 StartY=71.4 StartZ=0 EndX=22.5 EndY=71.4 EndZ=0
    g1: LineSegment StartX=22.5 StartY=71.4 StartZ=0 EndX=22.5 EndY=59 EndZ=0
    g2: LineSegment StartX=22.5 StartY=59 StartZ=0 EndX=6.7 EndY=59 EndZ=0
    g3: LineSegment StartX=6.7 StartY=59 StartZ=0 EndX=6.7 EndY=71.4 EndZ=0
  constraints (12):
    c: Coincident(g0,g1)
    c: Coincident(g1,g2)
    c: Coincident(g2,g3)
    c: Coincident(g3,g0)
    c: Horizontal(g0)
    c: Horizontal(g2)
    c: Vertical(g1)
    c: Vertical(g3)
    c: DistanceX(g0,g-3) = 0.2
    c: DistanceY(g-3,g0) = 0.2
    c: DistanceX(g-4,g1) = 0.2
    c: DistanceY(g1,g-4) = 0.2
FEATURE [PartDesign::Pocket] Pocket024
  BaseFeature = -> Pad019
  Length = 4
  Length2 = 100
  Profile = -> Sketch067
  Type = 0
FEATURE [PartDesign::Body] Body010  label="PSensor Cover"
  Group = -> [ShapeBinder020,Sketch066,Pad019,Sketch067,Pocket024]
  Origin = -> Origin010
  Placement = pos=(0,0,-8.2) rot=(0,0,1;0rad)
  Tip = -> Pocket024
FEATURE [PartDesign::ShapeBinder] ShapeBinder021
  Support = -> [Sketch032]
  TraceSupport = false
FEATURE [Sketcher::SketchObject] Sketch068
  ExternalGeometry = -> [ShapeBinder021]
  FullyConstrained = true
  MapMode = 5
  Support = -> [XY_Plane009]
  sketch-geometry (20):
    g0: LineSegment StartX=-17.3 StartY=-33.2 StartZ=0 EndX=-8.1 EndY=-33.2 EndZ=0
    g1: LineSegment StartX=-8.1 StartY=-42.4 StartZ=0 EndX=-17.3 EndY=-42.4 EndZ=0
    g2: LineSegment StartX=-17.3 StartY=-42.4 StartZ=0 EndX=-17.3 EndY=-33.2 EndZ=0
    g3: LineSegment StartX=-4.6 StartY=-20.5 StartZ=0 EndX=4.6 EndY=-20.5 EndZ=0
    g4: LineSegment StartX=4.6 StartY=-20.5 StartZ=0 EndX=4.6 EndY=-29.7 EndZ=0
    g5: LineSegment StartX=-4.6 StartY=-29.7 StartZ=0 EndX=-4.6 EndY=-20.5 EndZ=0
    g6: LineSegment StartX=8.1 StartY=-33.2 StartZ=0 EndX=17.3 EndY=-33.2 EndZ=0
    g7: LineSegment StartX=17.3 StartY=-33.2 StartZ=0 EndX=17.3 EndY=-42.4 EndZ=0
    g8: LineSegment StartX=17.3 StartY=-42.4 StartZ=0 EndX=8.1 EndY=-42.4 EndZ=0
    g9: LineSegment StartX=4.6 StartY=-46.3 StartZ=0 EndX=4.6 EndY=-55.5 EndZ=0
    g10: LineSegment StartX=4.6 StartY=-55.5 StartZ=0 EndX=-4.6 EndY=-55.5 EndZ=0
    g11: LineSegment StartX=-4.6 StartY=-55.5 StartZ=0 EndX=-4.6 EndY=-46.3 EndZ=0
    g12: LineSegment StartX=-8.1 StartY=-33.2 StartZ=0 EndX=-3.5 EndY=-37.8 EndZ=0
    g13: LineSegment StartX=-8.1 StartY=-42.4 StartZ=0 EndX=-3.5 EndY=-37.8 EndZ=0
    g14: LineSegment StartX=-4.6 StartY=-29.7 StartZ=0 EndX=0 EndY=-34.3 EndZ=0
    g15: LineSegment StartX=0 StartY=-34.3 StartZ=0 EndX=4.6 EndY=-29.7 EndZ=0
    g16: LineSegment StartX=8.1 StartY=-33.2 StartZ=0 EndX=3.5 EndY=-37.8 EndZ=0
    g17: LineSegment StartX=3.5 StartY=-37.8 StartZ=0 EndX=8.1 EndY=-42.4 EndZ=0
    g18: LineSegment StartX=-4.6 StartY=-46.3 StartZ=0 EndX=0 EndY=-41.7 EndZ=0
    g19: LineSegment StartX=0 StartY=-41.7 StartZ=0 EndX=4.6 EndY=-46.3 EndZ=0
  constraints (60):
    c: Coincident(g1,g2)
    c: Coincident(g2,g0)
    c: Horizontal(g0)
    c: Horizontal(g1)
    c: Vertical(g2)
    c: Coincident(g3,g4)
    c: Coincident(g5,g3)
    c: Horizontal(g3)
    c: Vertical(g4)
    c: Vertical(g5)
    c: Coincident(g6,g7)
    c: Coincident(g7,g8)
    c: Horizontal(g6)
    c: Horizontal(g8)
    c: Vertical(g7)
    c: Coincident(g9,g10)
    c: Coincident(g10,g11)
    c: Horizontal(g10)
    c: Vertical(g9)
    c: Vertical(g11)
    c: Vertical(g0,g1)
    c: Horizontal(g5,g4)
    c: Horizontal(g11,g9)
    c: Vertical(g6,g8)
    c: Coincident(g12,g0)
    c: Coincident(g13,g1)
    c: Coincident(g13,g12)
    c: Coincident(g14,g5)
    c: Coincident(g15,g14)
    c: Coincident(g15,g4)
    c: Coincident(g16,g6)
    c: Coincident(g17,g16)
    c: Coincident(g17,g8)
    c: Coincident(g18,g11)
    c: Coincident(g19,g18)
    c: Coincident(g19,g9)
    c: Equal(g0,g2)
    c: Equal(g1,g11)
    c: Equal(g11,g10)
    c: Equal(g9,g8)
    c: Equal(g8,g7)
    c: Equal(g6,g4)
    c: Equal(g4,g3)
    c: PointOnObject(g14,g-2)
    c: PointOnObject(g18,g-2)
    c: DistanceY(g7,g7) = 9.2
    c: Equal(g12,g14)
    c: Equal(g14,g16)
    c: Equal(g16,g19)
    c: Equal(g19,g18)
    c: Equal(g18,g13)
    c: Equal(g13,g15)
    c: Equal(g15,g17)
    c: Horizontal(g0,g6)
    c: DistanceY(g-3,g3) = 2.4
    c: DistanceY(g9,g-10) = 2.4
    c: DistanceX(g-8,g7) = 2.4
    c: DistanceX(g1,g-5) = 2.4
    c: DistanceY(g-8,g6) = 2.4
    c: Angle(g18) = 0.785398
FEATURE [Sketcher::SketchObject] Sketch069
  ExternalGeometry = -> [ShapeBinder021]
  FullyConstrained = true
  MapMode = 5
  Support = -> [XY_Plane009]
  sketch-geometry (20):
    g0: LineSegment StartX=-17 StartY=-30.8 StartZ=0 EndX=-7 EndY=-30.8 EndZ=0
    g1: LineSegment StartX=19 StartY=-32.8 StartZ=0 EndX=19 EndY=-42.8 EndZ=0
    g2: LineSegment StartX=17 StartY=-44.8 StartZ=0 EndX=7 EndY=-44.8 EndZ=0
    g3: LineSegment StartX=-19 StartY=-42.8 StartZ=0 EndX=-19 EndY=-32.8 EndZ=0
    g4: LineSegment StartX=-5 StartY=-18.8 StartZ=0 EndX=5 EndY=-18.8 EndZ=0
    g5: LineSegment StartX=7 StartY=-20.8 StartZ=0 EndX=7 EndY=-30.8 EndZ=0
    g6: LineSegment StartX=5 StartY=-56.8 StartZ=0 EndX=-5 EndY=-56.8 EndZ=0
    g7: LineSegment StartX=-7 StartY=-54.8 StartZ=0 EndX=-7 EndY=-44.8 EndZ=0
    g8: ArcOfCircle CenterX=-5 CenterY=-20.8 CenterZ=0 NormalX=0 NormalY=0 NormalZ=1 AngleXU=0 Radius=2 StartAngle=1.5708 EndAngle=3.14159
    g9: ArcOfCircle CenterX=5 CenterY=-20.8 CenterZ=0 NormalX=0 NormalY=0 NormalZ=1 AngleXU=0 Radius=2 StartAngle=0 EndAngle=1.5708
    g10: ArcOfCircle CenterX=17 CenterY=-32.8 CenterZ=0 NormalX=0 NormalY=0 NormalZ=1 AngleXU=0 Radius=2 StartAngle=6e-16 EndAngle=1.5708
    g11: ArcOfCircle CenterX=17 CenterY=-42.8 CenterZ=0 NormalX=0 NormalY=0 NormalZ=1 AngleXU=0 Radius=2 StartAngle=4.71239 EndAngle=6.28319
    g12: ArcOfCircle CenterX=5 CenterY=-54.8 CenterZ=0 NormalX=0 NormalY=0 NormalZ=1 AngleXU=0 Radius=2 StartAngle=4.71239 EndAngle=6.28318
    g13: ArcOfCircle CenterX=-5 CenterY=-54.8 CenterZ=0 NormalX=0 NormalY=0 NormalZ=1 AngleXU=0 Radius=2 StartAngle=3.14159 EndAngle=4.71239
    g14: ArcOfCircle CenterX=-17 CenterY=-42.8 CenterZ=0 NormalX=0 NormalY=0 NormalZ=1 AngleXU=0 Radius=2 StartAngle=3.14159 EndAngle=4.71239
    g15: ArcOfCircle CenterX=-17 CenterY=-32.8 CenterZ=0 NormalX=0 NormalY=0 NormalZ=1 AngleXU=0 Radius=2 StartAngle=1.5708 EndAngle=3.14159
    g16: LineSegment StartX=-7 StartY=-30.8 StartZ=0 EndX=-7 EndY=-20.8 EndZ=0
    g17: LineSegment StartX=7 StartY=-30.8 StartZ=0 EndX=17 EndY=-30.8 EndZ=0
    g18: LineSegment StartX=7 StartY=-44.8 StartZ=0 EndX=7 EndY=-54.8 EndZ=0
    g19: LineSegment StartX=-7 StartY=-44.8 StartZ=0 EndX=-17 EndY=-44.8 EndZ=0
  constraints (52):
    c: Horizontal(g0)
    c: Horizontal(g2)
    c: Vertical(g1)
    c: Vertical(g3)
    c: Horizontal(g4)
    c: Horizontal(g6)
    c: Vertical(g5)
    c: Vertical(g7)
    c: Tangent(g4,g8) = 1.5708
    c: Coincident(g16,g8) = 1.5708
    c: Tangent(g4,g9) = 1.5708
    c: Tangent(g5,g9) = 1.5708
    c: Coincident(g17,g10) = 1.5708
    c: Tangent(g1,g10) = 1.5708
    c: Tangent(g1,g11) = 1.5708
    c: Tangent(g2,g11) = 1.5708
    c: Coincident(g18,g12) = 1.5708
    c: Tangent(g6,g12) = 1.5708
    c: Tangent(g6,g13) = 1.5708
    c: Tangent(g7,g13) = 1.5708
    c: Coincident(g19,g14) = 1.5708
    c: Tangent(g3,g14) = 1.5708
    c: Tangent(g0,g15) = 1.5708
    c: Tangent(g3,g15) = 1.5708
    c: Tangent(g7,g16)
    c: Coincident(g0,g16)
    c: Tangent(g0,g17)
    c: Coincident(g5,g17)
    c: Tangent(g5,g18)
    c: Coincident(g2,g18)
    c: Coincident(g19,g7)
    c: Tangent(g2,g19)
    c: Equal(g14,g15)
    c: Equal(g15,g8)
    c: Equal(g8,g9)
    c: Equal(g9,g10)
    c: Equal(g10,g11)
    c: Equal(g11,g12)
    c: Equal(g12,g13)
    c: Radius(g9) = 2
    c: Equal(g1,g4)
    c: Equal(g4,g3)
    c: Equal(g3,g6)
    c: Equal(g1,g17)
    c: Equal(g17,g0)
    c: Equal(g0,g16)
    c: Equal(g16,g7)
    c: DistanceY(g1,g1) = 10
    c: Horizontal(g8,g8)
    c: Vertical(g14,g14)
    c: DistanceY(g-5,g10) = 2.8
    c: DistanceX(g13,g-6) = 2.8
FEATURE [PartDesign::Pad] Pad020
  Direction = (1,1,1)
  Length = 0.8
  Length2 = 100
  Profile = -> Sketch069
  Type = 0
FEATURE [PartDesign::Pad] Pad021
  BaseFeature = -> Pad020
  Direction = (1,1,1)
  Length = 3.4
  Length2 = 2
  Profile = -> Sketch068
  Type = 0
FEATURE [PartDesign::Body] Body009  label="Main Button"
  Group = -> [ShapeBinder021,Pad020,Sketch069,Sketch068,Pad021]
  Origin = -> Origin009
  Placement = pos=(0,0,-3) rot=(0,0,1;0rad)
  Tip = -> Pad021
FEATURE [Sketcher::SketchObject] Sketch070
  FullyConstrained = true
  MapMode = 5
  Placement = pos=(-3.34e-14,-75.8,1.67e-14) rot=(-0.57735,-0.57735,0.57735;4.18879rad)
  Support = -> [Pocket022]
  sketch-geometry (2):
    g0: Circle CenterX=6.4 CenterY=5 CenterZ=0 NormalX=0 NormalY=0 NormalZ=1 AngleXU=0 Radius=1.2
    g1: Circle CenterX=6.4 CenterY=-5 CenterZ=0 NormalX=0 NormalY=0 NormalZ=1 AngleXU=0 Radius=1.2
  constraints (5):
    c: Equal(g0,g1)
    c: Radius(g0) = 1.2
    c: Symmetric(g1,g0,g-1)
    c: DistanceY(g1,g0) = 10
    c: DistanceX(g-1,g1) = 6.4
FEATURE [PartDesign::Pocket] Pocket025
  BaseFeature = -> Pocket022
  Length = 5
  Length2 = 100
  Placement = pos=(0,0,0) rot=(0.57735,0.57735,0.57735;2.0944rad)
  Profile = -> Sketch070
  Type = 0
FEATURE [PartDesign::Body] Body006  label="Main Holder"
  Group = -> [ShapeBinder006,Sketch036,Pad006,Sketch040,Pocket010,ShapeBinder,ShapeBinder012,Sketch046,Pocket,Sketch047,Pocket016,Sketch048,Pad007,Sketch051,Pocket018,ShapeBinder018,Sketch063,Pocket021,Sketch064,Pocket022,Sketch070,Pocket025]
  Origin = -> Origin006
  Placement = pos=(0,0,0) rot=(1,0,0;-1.5708rad)
  Tip = -> Pocket025
FEATURE [Mesh::Feature] Mesh  label="Disp Holder (Meshed)"
FEATURE [Mesh::Feature] Mesh001  label="Main Holder (Meshed)"
FEATURE [Mesh::Feature] Mesh002  label="Main Cover (Meshed)"
FEATURE [Mesh::Feature] Mesh003  label="Main Button (Meshed)"
FEATURE [Mesh::Feature] Mesh004  label="PSensor Cover (Meshed)"
FEATURE [Sketcher::SketchObject] Sketch071
  ExternalGeometry = -> [Pocket020]
  FullyConstrained = true
  MapMode = 5
  Placement = pos=(0,0,3e-16) rot=(0,0,-1;1.5708rad)
  Support = -> [Pocket020]
  sketch-geometry (4):
    g0: LineSegment StartX=-75.8 StartY=61.5 StartZ=0 EndX=-4 EndY=61.5 EndZ=0
    g1: LineSegment StartX=-4 StartY=61.5 StartZ=0 EndX=-4 EndY=-61.5 EndZ=0
    g2: LineSegment StartX=-4 StartY=-61.5 StartZ=0 EndX=-75.8 EndY=-61.5 EndZ=0
    g3: LineSegment StartX=-75.8 StartY=-61.5 StartZ=0 EndX=-75.8 EndY=61.5 EndZ=0
  constraints (10):
    c: Coincident(g0,g1)
    c: Coincident(g1,g2)
    c: Coincident(g2,g3)
    c: Coincident(g3,g0)
    c: Horizontal(g0)
    c: Horizontal(g2)
    c: Vertical(g1)
    c: Vertical(g3)
    c: Coincident(g0,g-4)
    c: Coincident(g1,g-5)
FEATURE [PartDesign::Pocket] Pocket026
  BaseFeature = -> Pocket020
  Length = 0.4
  Length2 = 100
  Placement = pos=(0,0,0) rot=(0.57735,0.57735,0.57735;2.0944rad)
  Profile = -> Sketch071
  Type = 0
FEATURE [PartDesign::Body] Body005  label="Disp Holder"
  Group = -> [ShapeBinder005,Sketch035,Pad,Sketch037,Pocket007,Sketch038,Pocket008,Sketch039,Pocket009,ShapeBinder007,ShapeBinder008,ShapeBinder009,ShapeBinder010,ShapeBinder011,Sketch041,Pocket011,Sketch042,Pocket012,Sketch043,Pocket013,Sketch044,Pocket014,Sketch045,Pocket015,Chamfer,Sketch062,Pocket020,Sketch071,Pocket026]
  Origin = -> Origin005
  Tip = -> Pocket026
FEATURE [TechDraw::DrawViewPart] View  label="Top View"
  CoarseView = false
  Direction = (0,0,1)
  Focus = 100
  HardHidden = false
  IsoCount = 0
  IsoHidden = false
  IsoVisible = false
  LockPosition = false
  Perspective = false
  Rotation = 0
  ScaleType = 0
  SeamHidden = false
  SeamVisible = true
  SmoothHidden = false
  SmoothVisible = true
  Source = -> [Body005]
  X = 80
  XDirection = (1,0,0)
  Y = 125
FEATURE [TechDraw::DrawViewPart] View001  label="Bottom View"
  CoarseView = false
  Direction = (0,-1,0)
  Focus = 100
  HardHidden = false
  IsoCount = 0
  IsoHidden = false
  IsoVisible = false
  LockPosition = false
  Perspective = false
  Rotation = 0
  ScaleType = 0
  SeamHidden = false
  SeamVisible = true
  SmoothHidden = false
  SmoothVisible = true
  Source = -> [Body005]
  X = 80
  XDirection = (1,0,0)
  Y = 65
FEATURE [TechDraw::DrawViewPart] View002  label="Side"
  CoarseView = false
  Direction = (1,0,0)
  Focus = 100
  HardHidden = false
  IsoCount = 0
  IsoHidden = false
  IsoVisible = false
  LockPosition = false
  Perspective = false
  Rotation = 0
  ScaleType = 0
  SeamHidden = false
  SeamVisible = true
  SmoothHidden = false
  SmoothVisible = true
  Source = -> [Body005]
  X = 156
  XDirection = (-1,0,-1)
  Y = 125
FEATURE [TechDraw::DrawViewPart] View003  label="Up View"
  CoarseView = false
  Direction = (0,1,0)
  Focus = 100
  HardHidden = false
  IsoCount = 0
  IsoHidden = false
  IsoVisible = false
  LockPosition = false
  Perspective = false
  Rotation = 0
  ScaleType = 0
  SeamHidden = false
  SeamVisible = true
  SmoothHidden = false
  SmoothVisible = true
  Source = -> [Body005]
  X = 80
  XDirection = (1,0,0)
  Y = 185
FEATURE [TechDraw::DrawPage] Page  label="Page-Disp Holder"
  KeepUpdated = true
  NextBalloonIndex = 1
  ProjectionType = 0
  Template = -> Template
  Views = -> [View,View001,View002,View003]
